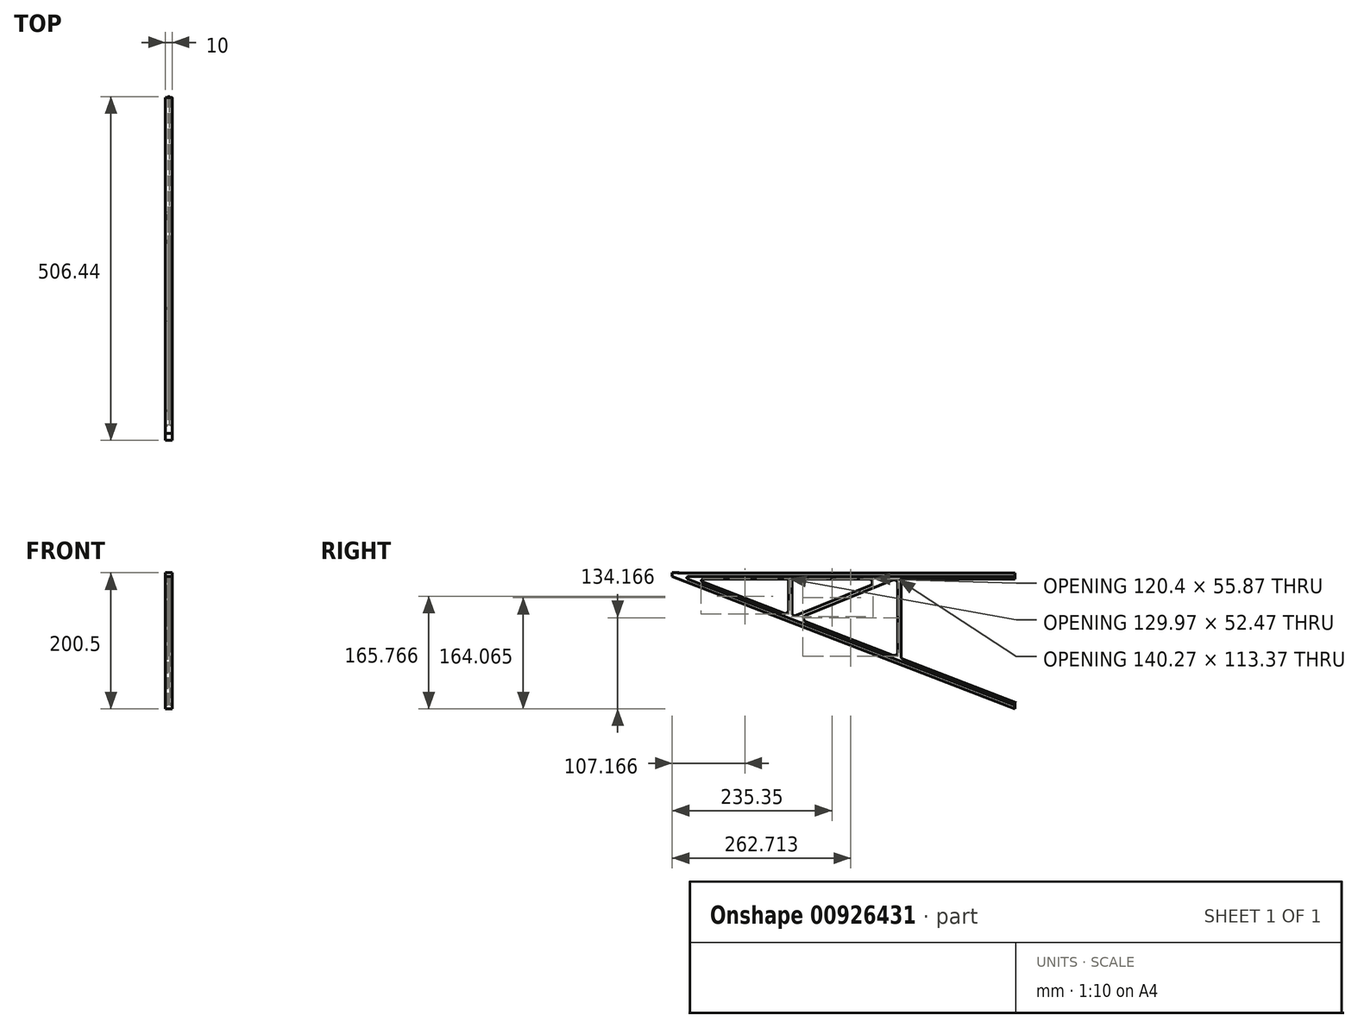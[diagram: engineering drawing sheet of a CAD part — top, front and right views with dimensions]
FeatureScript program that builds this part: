
annotation { "Feature Type Name" : "Feature", "Feature Type Description" : "" }
export const myFeature = defineFeature(function(context is Context, id is Id, definition is map)
    precondition{}
    {
        {
            var Q0;
            Q0=qCreatedBy(makeId("Front.planeOp"),FACE);
            var sketch = newSketch(context, id + "F0", { "sketchPlane" : qUnion([Q0])});
            skLineSegment(sketch, "E0", {"start": v(0, 0) * mm, "end": v(-5, 0) * mm});
            skLineSegment(sketch, "E1.MirrorCS", {"start": v(0, 0) * mm, "end": v(5, 0) * mm});
            skLineSegment(sketch, "E2", {"start": v(5, 0) * mm, "end": v(5, -200) * mm});
            skLineSegment(sketch, "E3.MirrorCS", {"start": v(-5, 0) * mm, "end": v(-5, -200) * mm});
            skLineSegment(sketch, "E4", {"start": v(5, -200) * mm, "end": v(-5, -200) * mm});
            skPoint(sketch, "E5", {"position": v(5, 0) * mm});
            skPoint(sketch, "E6", {"position": v(-5, 0) * mm});
            skSolve(sketch);
        }
        {
            var Q0;
            Q0=makeQuery(id+"F0.imprint","IMPRINT",FACE,{"disambiguationData":[TD([[makeQuery(id+"F0.imprint","IMPRINT",EDGE,{"derivedFrom":sQuery(id+"F0.wireOp",EDGE,"E0")}),1.0]])]});
            extrude(context, id + "F1", {"entities" : qUnion([Q0]), "depth" : 505 * mm, "offsetDistance" : 25 * mm});
        }
        {
            var Q0;
            Q0=qSketchRegion(id+"F0",true);
            extrude(context, id + "F2", {"entities" : qUnion([Q0]), "operationType" : NewBodyOperationType.ADD, "depth" : 500.5 * mm, "offsetDistance" : 25 * mm});
        }
        {
            var Q0;
            Q0=makeQuery(id+"F1.opExtrude","SWEPT_FACE",FACE,{"disambiguationData":[OSD([sQuery(id+"F0.wireOp",EDGE,"E3.MirrorCS")])]});
            var sketch = newSketch(context, id + "F3", { "sketchPlane" : qUnion([Q0])});
            skLineSegment(sketch, "E7", {"start": v(505, 0) * mm, "end": v(505, -5) * mm});
            skLineSegment(sketch, "E8", {"start": v(0, 0) * mm, "end": v(0, -5) * mm});
            skLineSegment(sketch, "E9", {"start": v(0, -5) * mm, "end": v(505, -5) * mm});
            skLineSegment(sketch, "E10", {"start": v(0, -200) * mm, "end": v(0, -195) * mm});
            skLineSegment(sketch, "E11", {"start": v(0, -195) * mm, "end": v(505, 0) * mm});
            skLineSegment(sketch, "E12", {"start": v(0, -200) * mm, "end": v(505, -5) * mm});
            skPoint(sketch, "E13", {"position": v(492.05, -5) * mm});
            skLineSegment(sketch, "E14", {"start": v(492.05, -5) * mm, "end": v(331.35, -5) * mm});
            skLineSegment(sketch, "E15", {"start": v(331.35, -5) * mm, "end": v(333.85, -5) * mm});
            skLineSegment(sketch, "E16", {"start": v(331.35, -5) * mm, "end": v(328.85, -5) * mm});
            skLineSegment(sketch, "E17", {"start": v(328.85, -5) * mm, "end": v(328.85, -68.02) * mm});
            skLineSegment(sketch, "E18", {"start": v(333.85, -5) * mm, "end": v(333.85, -66.09) * mm});
            skLineSegment(sketch, "E19", {"start": v(331.35, -5) * mm, "end": v(170.65, -5) * mm});
            skLineSegment(sketch, "E20", {"start": v(170.65, -5) * mm, "end": v(173.15, -5) * mm});
            skLineSegment(sketch, "E21", {"start": v(170.65, -5) * mm, "end": v(168.15, -5) * mm});
            skLineSegment(sketch, "E22", {"start": v(168.15, -5) * mm, "end": v(168.15, -130.07) * mm});
            skLineSegment(sketch, "E23", {"start": v(173.15, -5) * mm, "end": v(173.15, -128.14) * mm});
            skLineSegment(sketch, "E24", {"start": v(331.35, -5) * mm, "end": v(331.35, -83.15) * mm});
            skLineSegment(sketch, "E25", {"start": v(173.15, -5) * mm, "end": v(328.85, -68.02) * mm});
            skLineSegment(sketch, "E26", {"start": v(328.85, -68.02) * mm, "end": v(331.35, -69.03) * mm});
            skLineSegment(sketch, "E27", {"start": v(328.85, -68.02) * mm, "end": v(327.91, -70.34) * mm});
            skLineSegment(sketch, "E28", {"start": v(327.91, -70.34) * mm, "end": v(328.85, -68.02) * mm});
            skLineSegment(sketch, "E29", {"start": v(328.85, -68.02) * mm, "end": v(329.79, -65.7) * mm});
            skLineSegment(sketch, "E30", {"start": v(173.15, -5) * mm, "end": v(174.09, -2.68) * mm});
            skLineSegment(sketch, "E31", {"start": v(173.15, -5) * mm, "end": v(172.21, -7.32) * mm});
            skLineSegment(sketch, "E32", {"start": v(174.09, -2.68) * mm, "end": v(329.79, -65.7) * mm});
            skLineSegment(sketch, "E33", {"start": v(172.21, -7.32) * mm, "end": v(327.91, -70.34) * mm});
            skSolve(sketch);
        }
        {
            var Q0;
            {var subQ0=sQuery(id+"F3.wireOp",EDGE,"E17");var subQ1=sQuery(id+"F3.wireOp",EDGE,"E9");var subQ2=makeQuery(id+"F3.imprint","INTERSECT",VERTEX,{"derivedFrom":[subQ1,subQ0]});Q0=makeQuery(id+"F3.imprint","IMPRINT",FACE,{"disambiguationData":[TD([[makeQuery(id+"F3.imprint","IMPRINT",EDGE,{"disambiguationData":[TD([[subQ2,1.0]])],"derivedFrom":subQ1}),-1.0]])]});}
            var Q1;
            {var subQ0=sQuery(id+"F3.wireOp",EDGE,"E23");var subQ1=sQuery(id+"F3.wireOp",EDGE,"E11");var subQ2=makeQuery(id+"F3.imprint","INTERSECT",VERTEX,{"derivedFrom":[subQ1,subQ0]});Q1=makeQuery(id+"F3.imprint","IMPRINT",FACE,{"disambiguationData":[TD([[makeQuery(id+"F3.imprint","IMPRINT",EDGE,{"disambiguationData":[TD([[subQ2,-1.0]])],"derivedFrom":subQ1}),1.0]])]});}
            var Q2;
            {var subQ3=sQuery(id+"F3.wireOp",EDGE,"E22");Q2=makeQuery(id+"F3.imprint","IMPRINT",FACE,{"disambiguationData":[TD([[makeQuery(id+"F3.imprint","IMPRINT",EDGE,{"derivedFrom":subQ3}),-1.0]])]});}
            var Q3;
            {var subQ0=sQuery(id+"F3.wireOp",EDGE,"E18");Q3=makeQuery(id+"F3.imprint","IMPRINT",FACE,{"disambiguationData":[TD([[makeQuery(id+"F3.imprint","IMPRINT",EDGE,{"derivedFrom":subQ0}),1.0]])]});}
            extrude(context, id + "F4", {"entities" : qUnion([Q0, Q1, Q2, Q3]), "operationType" : NewBodyOperationType.REMOVE, "endBound" : BoundingType.UP_TO_NEXT, "oppositeDirection" : true, "depth" : 25 * mm, "offsetDistance" : 25 * mm});
        }
        {
            var Q0;
            {var subQ1=sQuery(id+"F0.wireOp",EDGE,"E3.MirrorCS");var subQ2=makeQuery(id+"F1.opExtrude","SWEPT_EDGE",EDGE,{"disambiguationData":[OSD([subQ1,sQuery(id+"F0.wireOp",EDGE,"E4")])]});Q0=makeQuery(id+"F3.imprint","IMPRINT",FACE,{"disambiguationData":[TD([[makeQuery(id+"F3.imprint","IMPRINT",EDGE,{"derivedFrom":subQ2}),-1.0]])]});}
            extrude(context, id + "F5", {"entities" : qUnion([Q0]), "operationType" : NewBodyOperationType.REMOVE, "endBound" : BoundingType.UP_TO_NEXT, "oppositeDirection" : true, "depth" : 25 * mm, "offsetDistance" : 25 * mm});
        }
        {
            var Q0;
            Q0=makeQuery(id+"F1.opExtrude","SWEPT_FACE",FACE,{"disambiguationData":[OSD([sQuery(id+"F0.wireOp",EDGE,"E3.MirrorCS")])]});
            var sketch = newSketch(context, id + "F6", { "sketchPlane" : qUnion([Q0])});
            skLineSegment(sketch, "E34", {"start": v(168.15, -5) * mm, "end": v(179.81, -5) * mm});
            skLineSegment(sketch, "E35", {"start": v(328.85, -5) * mm, "end": v(333.85, -5) * mm});
            skLineSegment(sketch, "E36", {"start": v(325.44, -69.33) * mm, "end": v(333.85, -66.09) * mm});
            skLineSegment(sketch, "E37", {"start": v(168.15, -130.07) * mm, "end": v(173.15, -128.14) * mm});
            skSolve(sketch);
        }
        {
            var Q0;
            Q0=makeQuery(id+"F6.imprint","IMPRINT",FACE,{"disambiguationData":[TD([[makeQuery(id+"F6.imprint","IMPRINT",EDGE,{"derivedFrom":sQuery(id+"F6.wireOp",EDGE,"E34")}),-1.0]])]});
            extrude(context, id + "F7", {"entities" : qUnion([Q0]), "operationType" : NewBodyOperationType.REMOVE, "oppositeDirection" : true, "depth" : 3.5 * mm, "offsetDistance" : 25 * mm});
        }
        {
            var Q0;
            Q0=makeQuery(id+"F1.opExtrude","SWEPT_FACE",FACE,{"disambiguationData":[OSD([sQuery(id+"F0.wireOp",EDGE,"E0"),sQuery(id+"F0.wireOp",EDGE,"E1.MirrorCS")])]});
            var sketch = newSketch(context, id + "F8", { "sketchPlane" : qUnion([Q0])});
            skLineSegment(sketch, "E38.bottom", {"start": v(-5, -505) * mm, "end": v(5, -505) * mm});
            skLineSegment(sketch, "E38.top", {"start": v(-5, -495) * mm, "end": v(5, -495) * mm});
            skLineSegment(sketch, "E38.left", {"start": v(-5, -505) * mm, "end": v(-5, -495) * mm});
            skLineSegment(sketch, "E38.right", {"start": v(5, -505) * mm, "end": v(5, -495) * mm});
            skSolve(sketch);
        }
        {
            var Q0;
            Q0=makeQuery(id+"F1.opExtrude","SWEPT_FACE",FACE,{"disambiguationData":[OSD([sQuery(id+"F0.wireOp",EDGE,"E2")])]});
            var sketch = newSketch(context, id + "F9", { "sketchPlane" : qUnion([Q0])});
            skLineSegment(sketch, "E39", {"start": v(-173.15, -128.14) * mm, "end": v(-168.15, -130.07) * mm});
            skLineSegment(sketch, "E40", {"start": v(-325.44, -69.33) * mm, "end": v(-333.85, -66.09) * mm});
            skLineSegment(sketch, "E41", {"start": v(-333.85, -5) * mm, "end": v(-328.85, -5) * mm});
            skLineSegment(sketch, "E42", {"start": v(-168.15, -5) * mm, "end": v(-179.81, -5) * mm});
            skSolve(sketch);
        }
        {
            var Q0;
            Q0=makeQuery(id+"F8.imprint","IMPRINT",FACE,{"disambiguationData":[TD([[makeQuery(id+"F8.imprint","IMPRINT",EDGE,{"derivedFrom":sQuery(id+"F8.wireOp",EDGE,"E38.bottom")}),1.0]])]});
            extrude(context, id + "F10", {"entities" : qUnion([Q0]), "operationType" : NewBodyOperationType.ADD, "depth" : 0.5 * mm, "offsetDistance" : 25 * mm});
        }
        {
            var Q0;
            Q0=makeQuery(id+"F9.imprint","IMPRINT",FACE,{"disambiguationData":[TD([[makeQuery(id+"F9.imprint","IMPRINT",EDGE,{"derivedFrom":sQuery(id+"F9.wireOp",EDGE,"E39")}),1.0]])]});
            extrude(context, id + "F11", {"entities" : qUnion([Q0]), "operationType" : NewBodyOperationType.REMOVE, "oppositeDirection" : true, "depth" : 3.5 * mm, "offsetDistance" : 25 * mm});
        }
        {
            var Q0;
            {var subQ0=sQuery(id+"F3.wireOp",EDGE,"E9");Q0=makeQuery(id+"F11.boolean.opBoolean","MERGE",FACE,{"derivedFrom":[makeQuery(id+"F7.boolean.opBoolean","MERGE",FACE,{"derivedFrom":[makeQuery(id+"F4.boolean.opBoolean","COPY",FACE,{"derivedFrom":makeQuery(id+"F4.opExtrude","SWEPT_FACE",FACE,{"disambiguationData":[OSD([subQ0]),TDD([makeQuery(id+"F3.imprint","IMPRINT",EDGE,{"disambiguationData":[TD([[makeQuery(id+"F3.imprint","INTERSECT",VERTEX,{"derivedFrom":[subQ0,sQuery(id+"F3.wireOp",EDGE,"E22")]}),1.0]])],"derivedFrom":subQ0})])]})}),makeQuery(id+"F4.boolean.opBoolean","COPY",FACE,{"derivedFrom":makeQuery(id+"F4.opExtrude","SWEPT_FACE",FACE,{"disambiguationData":[OSD([subQ0]),TDD([makeQuery(id+"F3.imprint","IMPRINT",EDGE,{"disambiguationData":[TD([[makeQuery(id+"F3.imprint","INTERSECT",VERTEX,{"derivedFrom":[subQ0,sQuery(id+"F3.wireOp",EDGE,"E18")]}),-1.0]])],"derivedFrom":subQ0})])]})}),makeQuery(id+"F4.boolean.opBoolean","COPY",FACE,{"derivedFrom":makeQuery(id+"F4.opExtrude","SWEPT_FACE",FACE,{"disambiguationData":[OSD([subQ0]),TDD([makeQuery(id+"F3.imprint","IMPRINT",EDGE,{"disambiguationData":[TD([[makeQuery(id+"F3.imprint","INTERSECT",VERTEX,{"derivedFrom":[subQ0,sQuery(id+"F3.wireOp",EDGE,"E17")]}),1.0]])],"derivedFrom":subQ0})])]})})],"fromTools":[makeQuery(id+"F7.opExtrude","SWEPT_FACE",FACE,{"disambiguationData":[OSD([sQuery(id+"F6.wireOp",EDGE,"E34")])]}),makeQuery(id+"F7.opExtrude","SWEPT_FACE",FACE,{"disambiguationData":[OSD([sQuery(id+"F6.wireOp",EDGE,"E35")])]})]})],"fromTools":[makeQuery(id+"F11.opExtrude","SWEPT_FACE",FACE,{"disambiguationData":[OSD([sQuery(id+"F9.wireOp",EDGE,"E41")])]}),makeQuery(id+"F11.opExtrude","SWEPT_FACE",FACE,{"disambiguationData":[OSD([sQuery(id+"F9.wireOp",EDGE,"E42")])]})]});}
            var sketch = newSketch(context, id + "F12", { "sketchPlane" : qUnion([Q0])});
            skLineSegment(sketch, "E43", {"start": v(1.5, 0) * mm, "end": v(1.5, 492.05) * mm});
            skLineSegment(sketch, "E44", {"start": v(-1.5, 0) * mm, "end": v(1.5, 0) * mm});
            skLineSegment(sketch, "E45", {"start": v(-1.5, 0) * mm, "end": v(-1.5, 492.05) * mm});
            skLineSegment(sketch, "E46", {"start": v(1.5, 492.05) * mm, "end": v(-1.5, 492.05) * mm});
            skSolve(sketch);
        }
        {
            var Q0;
            {var subQ3=sQuery(id+"F12.wireOp",EDGE,"E46");Q0=makeQuery(id+"F12.imprint","IMPRINT",FACE,{"disambiguationData":[TD([[makeQuery(id+"F12.imprint","IMPRINT",EDGE,{"derivedFrom":subQ3}),1.0]])]});}
            var Q1;
            {var subQ1=sQuery(id+"F3.wireOp",EDGE,"E9");var subQ2=makeQuery(id+"F4.boolean.opBoolean","COPY",EDGE,{"derivedFrom":makeQuery(id+"F4.opExtrude","SWEPT_EDGE",EDGE,{"disambiguationData":[OSD([subQ1,sQuery(id+"F3.wireOp",EDGE,"E17")])]})});Q1=makeQuery(id+"F12.imprint","IMPRINT",FACE,{"disambiguationData":[TD([[makeQuery(id+"F12.imprint","IMPRINT",EDGE,{"derivedFrom":subQ2}),1.0]])]});}
            var Q2;
            {var subQ3=sQuery(id+"F12.wireOp",EDGE,"E44");Q2=makeQuery(id+"F12.imprint","IMPRINT",FACE,{"disambiguationData":[TD([[makeQuery(id+"F12.imprint","IMPRINT",EDGE,{"derivedFrom":subQ3}),-1.0]])]});}
            extrude(context, id + "F13", {"entities" : qUnion([Q0, Q1, Q2]), "operationType" : NewBodyOperationType.ADD, "depth" : 4 * mm, "offsetDistance" : 25 * mm});
        }
        {
            var Q0;
            {var subQ0=sQuery(id+"F3.wireOp",EDGE,"E11");Q0=makeQuery(id+"F11.boolean.opBoolean","MERGE",FACE,{"derivedFrom":[makeQuery(id+"F7.boolean.opBoolean","MERGE",FACE,{"derivedFrom":[makeQuery(id+"F4.boolean.opBoolean","COPY",FACE,{"derivedFrom":makeQuery(id+"F4.opExtrude","SWEPT_FACE",FACE,{"disambiguationData":[OSD([subQ0]),TDD([makeQuery(id+"F3.imprint","IMPRINT",EDGE,{"disambiguationData":[TD([[makeQuery(id+"F3.imprint","INTERSECT",VERTEX,{"derivedFrom":[subQ0,sQuery(id+"F3.wireOp",EDGE,"E22")]}),1.0]])],"derivedFrom":subQ0})])]})}),makeQuery(id+"F4.boolean.opBoolean","COPY",FACE,{"derivedFrom":makeQuery(id+"F4.opExtrude","SWEPT_FACE",FACE,{"disambiguationData":[OSD([subQ0]),TDD([makeQuery(id+"F3.imprint","IMPRINT",EDGE,{"disambiguationData":[TD([[makeQuery(id+"F3.imprint","INTERSECT",VERTEX,{"derivedFrom":[subQ0,sQuery(id+"F3.wireOp",EDGE,"E18")]}),-1.0]])],"derivedFrom":subQ0})])]})}),makeQuery(id+"F4.boolean.opBoolean","COPY",FACE,{"derivedFrom":makeQuery(id+"F4.opExtrude","SWEPT_FACE",FACE,{"disambiguationData":[OSD([subQ0]),TDD([makeQuery(id+"F3.imprint","IMPRINT",EDGE,{"disambiguationData":[TD([[makeQuery(id+"F3.imprint","INTERSECT",VERTEX,{"derivedFrom":[subQ0,sQuery(id+"F3.wireOp",EDGE,"E23")]}),-1.0]])],"derivedFrom":subQ0})])]})})],"fromTools":[makeQuery(id+"F7.opExtrude","SWEPT_FACE",FACE,{"disambiguationData":[OSD([sQuery(id+"F6.wireOp",EDGE,"E36")])]}),makeQuery(id+"F7.opExtrude","SWEPT_FACE",FACE,{"disambiguationData":[OSD([sQuery(id+"F6.wireOp",EDGE,"E37")])]})]})],"fromTools":[makeQuery(id+"F11.opExtrude","SWEPT_FACE",FACE,{"disambiguationData":[OSD([sQuery(id+"F9.wireOp",EDGE,"E39")])]}),makeQuery(id+"F11.opExtrude","SWEPT_FACE",FACE,{"disambiguationData":[OSD([sQuery(id+"F9.wireOp",EDGE,"E40")])]})]});}
            var sketch = newSketch(context, id + "F14", { "sketchPlane" : qUnion([Q0])});
            skLineSegment(sketch, "E47", {"start": v(-1.5, 70.24) * mm, "end": v(-1.5, -457.22) * mm});
            skLineSegment(sketch, "E48", {"start": v(1.5, 70.24) * mm, "end": v(1.5, -457.22) * mm});
            skLineSegment(sketch, "E49", {"start": v(1.5, -457.22) * mm, "end": v(-1.5, -457.22) * mm});
            skLineSegment(sketch, "E50", {"start": v(1.5, 70.24) * mm, "end": v(-1.5, 70.24) * mm});
            skSolve(sketch);
        }
        {
            var Q0;
            {var subQ3=sQuery(id+"F14.wireOp",EDGE,"E50");Q0=makeQuery(id+"F14.imprint","IMPRINT",FACE,{"disambiguationData":[TD([[makeQuery(id+"F14.imprint","IMPRINT",EDGE,{"derivedFrom":subQ3}),1.0]])]});}
            var Q1;
            {var subQ1=sQuery(id+"F3.wireOp",EDGE,"E11");var subQ2=makeQuery(id+"F4.boolean.opBoolean","COPY",EDGE,{"derivedFrom":makeQuery(id+"F4.opExtrude","SWEPT_EDGE",EDGE,{"disambiguationData":[OSD([subQ1,sQuery(id+"F3.wireOp",EDGE,"E23")])]})});Q1=makeQuery(id+"F14.imprint","IMPRINT",FACE,{"disambiguationData":[TD([[makeQuery(id+"F14.imprint","IMPRINT",EDGE,{"derivedFrom":subQ2}),1.0]])]});}
            var Q2;
            {var subQ1=sQuery(id+"F3.wireOp",EDGE,"E18");var subQ2=sQuery(id+"F3.wireOp",EDGE,"E11");var subQ3=makeQuery(id+"F4.boolean.opBoolean","COPY",EDGE,{"derivedFrom":makeQuery(id+"F4.opExtrude","SWEPT_EDGE",EDGE,{"disambiguationData":[OSD([subQ2,subQ1])]})});Q2=makeQuery(id+"F14.imprint","IMPRINT",FACE,{"disambiguationData":[TD([[makeQuery(id+"F14.imprint","IMPRINT",EDGE,{"derivedFrom":subQ3}),1.0]])]});}
            extrude(context, id + "F15", {"entities" : qUnion([Q0, Q1, Q2]), "operationType" : NewBodyOperationType.ADD, "depth" : 4 * mm, "offsetDistance" : 25 * mm});
        }
        {
            var Q0;
            Q0=makeQuery(id+"F15.opExtrude","SWEPT_FACE",FACE,{"disambiguationData":[OSD([sQuery(id+"F3.wireOp",EDGE,"E11"),sQuery(id+"F3.wireOp",EDGE,"E22")])]});
            extrude(context, id + "F16", {"entities" : qUnion([Q0]), "operationType" : NewBodyOperationType.ADD, "depth" : 40 * mm, "offsetDistance" : 25 * mm});
        }
        {
            var Q0;
            {var subQ0=sQuery(id+"F12.wireOp",EDGE,"E46");var subQ1=sQuery(id+"F12.wireOp",EDGE,"E45");var subQ2=sQuery(id+"F12.wireOp",EDGE,"E43");var subQ3=sQuery(id+"F3.wireOp",EDGE,"E18");var subQ4=sQuery(id+"F3.wireOp",EDGE,"E9");Q0=makeQuery(id+"F15.boolean.opBoolean","INTERSECT",EDGE,{"derivedFrom":[makeQuery(id+"F13.opExtrude","CAP_FACE",FACE,{"disambiguationData":[OSD([subQ4,subQ3,subQ2,subQ1,subQ0])],"isStart":false}),makeQuery(id+"F15.opExtrude","CAP_FACE",FACE,{"disambiguationData":[OSD([subQ4,sQuery(id+"F3.wireOp",EDGE,"E11"),subQ3,sQuery(id+"F6.wireOp",EDGE,"E36"),sQuery(id+"F6.wireOp",EDGE,"E37"),sQuery(id+"F9.wireOp",EDGE,"E39"),sQuery(id+"F9.wireOp",EDGE,"E40"),subQ2,subQ1,subQ0,sQuery(id+"F14.wireOp",EDGE,"E47"),sQuery(id+"F14.wireOp",EDGE,"E48")])],"isStart":false})]});}
            var Q1;
            {var subQ6=sQuery(id+"F3.wireOp",EDGE,"E11");var subQ7=sQuery(id+"F3.wireOp",EDGE,"E9");var subQ10=makeQuery(id+"F4.boolean.opBoolean","COPY",EDGE,{"derivedFrom":makeQuery(id+"F4.opExtrude","SWEPT_EDGE",EDGE,{"disambiguationData":[OSD([subQ7,subQ6])]})});var subQ11=sQuery(id+"F0.wireOp",EDGE,"E3.MirrorCS");Q1=makeQuery(id+"F13.boolean.opBoolean","SPLIT",EDGE,{"disambiguationData":[TD([makeQuery(id+"F1.opExtrude","SWEPT_FACE",FACE,{"disambiguationData":[OSD([subQ11])]})])],"derivedFrom":subQ10});}
            var Q2;
            {var subQ1=sQuery(id+"F3.wireOp",EDGE,"E11");var subQ9=sQuery(id+"F3.wireOp",EDGE,"E9");var subQ13=makeQuery(id+"F4.boolean.opBoolean","COPY",EDGE,{"derivedFrom":makeQuery(id+"F4.opExtrude","SWEPT_EDGE",EDGE,{"disambiguationData":[OSD([subQ9,subQ1])]})});Q2=makeQuery(id+"F13.boolean.opBoolean","SPLIT",EDGE,{"disambiguationData":[TD([makeQuery(id+"F1.opExtrude","SWEPT_FACE",FACE,{"disambiguationData":[OSD([sQuery(id+"F0.wireOp",EDGE,"E2")])]})])],"derivedFrom":subQ13});}
            fillet(context, id + "F17", {"entities" : qUnion([Q0, Q1, Q2]), "radius" : 2 * mm, "tangentPropagation" : true, "allowEdgeOverflow" : false});
        }
        {
            var Q0;
            Q0=makeQuery(id+"F13.opExtrude","CAP_EDGE",EDGE,{"disambiguationData":[OSD([sQuery(id+"F3.wireOp",EDGE,"E9"),sQuery(id+"F3.wireOp",EDGE,"E18")])],"isStart":false});
            var Q1;
            Q1=makeQuery(id+"F13.opExtrude","CAP_EDGE",EDGE,{"disambiguationData":[OSD([sQuery(id+"F3.wireOp",EDGE,"E9"),sQuery(id+"F3.wireOp",EDGE,"E17")])],"isStart":false});
            var Q2;
            Q2=makeQuery(id+"F4.boolean.opBoolean","COPY",EDGE,{"derivedFrom":makeQuery(id+"F4.opExtrude","SWEPT_EDGE",EDGE,{"disambiguationData":[OSD([sQuery(id+"F3.wireOp",EDGE,"E17"),sQuery(id+"F3.wireOp",EDGE,"E32")])]})});
            var Q3;
            {var subQ0=sQuery(id+"F3.wireOp",EDGE,"E18");Q3=makeQuery(id+"F15.boolean.opBoolean","INTERSECT",EDGE,{"derivedFrom":[makeQuery(id+"F4.boolean.opBoolean","COPY",FACE,{"derivedFrom":makeQuery(id+"F4.opExtrude","SWEPT_FACE",FACE,{"disambiguationData":[OSD([subQ0])]})}),makeQuery(id+"F15.opExtrude","CAP_FACE",FACE,{"disambiguationData":[OSD([sQuery(id+"F3.wireOp",EDGE,"E9"),sQuery(id+"F3.wireOp",EDGE,"E11"),subQ0,sQuery(id+"F6.wireOp",EDGE,"E36"),sQuery(id+"F6.wireOp",EDGE,"E37"),sQuery(id+"F9.wireOp",EDGE,"E39"),sQuery(id+"F9.wireOp",EDGE,"E40"),sQuery(id+"F12.wireOp",EDGE,"E43"),sQuery(id+"F12.wireOp",EDGE,"E45"),sQuery(id+"F12.wireOp",EDGE,"E46"),sQuery(id+"F14.wireOp",EDGE,"E47"),sQuery(id+"F14.wireOp",EDGE,"E48")])],"isStart":false})]});}
            var Q4;
            {var subQ0=sQuery(id+"F3.wireOp",EDGE,"E32");Q4=makeQuery(id+"F13.boolean.opBoolean","INTERSECT",EDGE,{"derivedFrom":[makeQuery(id+"F4.boolean.opBoolean","COPY",FACE,{"derivedFrom":makeQuery(id+"F4.opExtrude","SWEPT_FACE",FACE,{"disambiguationData":[OSD([subQ0])]})}),makeQuery(id+"F13.opExtrude","CAP_FACE",FACE,{"disambiguationData":[OSD([sQuery(id+"F3.wireOp",EDGE,"E9"),sQuery(id+"F3.wireOp",EDGE,"E17"),subQ0,sQuery(id+"F12.wireOp",EDGE,"E43"),sQuery(id+"F12.wireOp",EDGE,"E45")])],"isStart":false})]});}
            var Q5;
            Q5=makeQuery(id+"F4.boolean.opBoolean","COPY",EDGE,{"derivedFrom":makeQuery(id+"F4.opExtrude","SWEPT_EDGE",EDGE,{"disambiguationData":[OSD([sQuery(id+"F3.wireOp",EDGE,"E23"),sQuery(id+"F3.wireOp",EDGE,"E33")])]})});
            var Q6;
            Q6=makeQuery(id+"F13.opExtrude","CAP_EDGE",EDGE,{"disambiguationData":[OSD([sQuery(id+"F3.wireOp",EDGE,"E9"),sQuery(id+"F3.wireOp",EDGE,"E22")])],"isStart":false});
            var Q7;
            {var subQ0=sQuery(id+"F3.wireOp",EDGE,"E23");Q7=makeQuery(id+"F15.boolean.opBoolean","INTERSECT",EDGE,{"derivedFrom":[makeQuery(id+"F4.boolean.opBoolean","COPY",FACE,{"derivedFrom":makeQuery(id+"F4.opExtrude","SWEPT_FACE",FACE,{"disambiguationData":[OSD([subQ0])]})}),makeQuery(id+"F15.opExtrude","CAP_FACE",FACE,{"disambiguationData":[OSD([sQuery(id+"F3.wireOp",EDGE,"E11"),subQ0,sQuery(id+"F3.wireOp",EDGE,"E33"),sQuery(id+"F14.wireOp",EDGE,"E47"),sQuery(id+"F14.wireOp",EDGE,"E48")])],"isStart":false})]});}
            var Q8;
            {var subQ0=sQuery(id+"F3.wireOp",EDGE,"E22");var subQ1=sQuery(id+"F3.wireOp",EDGE,"E11");Q8=makeQuery(id+"F16.boolean.opBoolean","INTERSECT",EDGE,{"derivedFrom":[makeQuery(id+"F4.boolean.opBoolean","COPY",FACE,{"derivedFrom":makeQuery(id+"F4.opExtrude","SWEPT_FACE",FACE,{"disambiguationData":[OSD([subQ0])]})}),makeQuery(id+"F16.opExtrude","SWEPT_FACE",FACE,{"disambiguationData":[OSD([subQ1,subQ0]),TDD([makeQuery(id+"F15.opExtrude","CAP_EDGE",EDGE,{"disambiguationData":[OSD([subQ1,subQ0])],"isStart":false})])]})]});}
            var Q9;
            {var subQ0=sQuery(id+"F3.wireOp",EDGE,"E33");Q9=makeQuery(id+"F15.boolean.opBoolean","INTERSECT",EDGE,{"derivedFrom":[makeQuery(id+"F4.boolean.opBoolean","COPY",FACE,{"derivedFrom":makeQuery(id+"F4.opExtrude","SWEPT_FACE",FACE,{"disambiguationData":[OSD([subQ0])]})}),makeQuery(id+"F15.opExtrude","CAP_FACE",FACE,{"disambiguationData":[OSD([sQuery(id+"F3.wireOp",EDGE,"E11"),sQuery(id+"F3.wireOp",EDGE,"E23"),subQ0,sQuery(id+"F14.wireOp",EDGE,"E47"),sQuery(id+"F14.wireOp",EDGE,"E48")])],"isStart":false})]});}
            fillet(context, id + "F18", {"entities" : qUnion([Q0, Q1, Q2, Q3, Q4, Q5, Q6, Q7, Q8, Q9]), "radius" : 5 * mm, "tangentPropagation" : true, "allowEdgeOverflow" : false});
        }
        {
            var Q0;
            {var subQ0=sQuery(id+"F14.wireOp",EDGE,"E47");var subQ1=sQuery(id+"F3.wireOp",EDGE,"E22");var subQ2=sQuery(id+"F3.wireOp",EDGE,"E11");var subQ5=sQuery(id+"F3.wireOp",EDGE,"E18");var subQ7=sQuery(id+"F12.wireOp",EDGE,"E45");var subQ8=sQuery(id+"F3.wireOp",EDGE,"E9");var subQ9=sQuery(id+"F6.wireOp",EDGE,"E37");var subQ10=sQuery(id+"F6.wireOp",EDGE,"E36");var subQ11=sQuery(id+"F3.wireOp",EDGE,"E23");var subQ13=makeQuery(id+"F11.boolean.opBoolean","MERGE",FACE,{"derivedFrom":[makeQuery(id+"F7.boolean.opBoolean","MERGE",FACE,{"derivedFrom":[makeQuery(id+"F4.boolean.opBoolean","COPY",FACE,{"derivedFrom":makeQuery(id+"F4.opExtrude","SWEPT_FACE",FACE,{"disambiguationData":[OSD([subQ2]),TDD([makeQuery(id+"F3.imprint","IMPRINT",EDGE,{"disambiguationData":[TD([[makeQuery(id+"F3.imprint","INTERSECT",VERTEX,{"derivedFrom":[subQ2,subQ1]}),1.0]])],"derivedFrom":subQ2})])]})}),makeQuery(id+"F4.boolean.opBoolean","COPY",FACE,{"derivedFrom":makeQuery(id+"F4.opExtrude","SWEPT_FACE",FACE,{"disambiguationData":[OSD([subQ2]),TDD([makeQuery(id+"F3.imprint","IMPRINT",EDGE,{"disambiguationData":[TD([[makeQuery(id+"F3.imprint","INTERSECT",VERTEX,{"derivedFrom":[subQ2,subQ5]}),-1.0]])],"derivedFrom":subQ2})])]})}),makeQuery(id+"F4.boolean.opBoolean","COPY",FACE,{"derivedFrom":makeQuery(id+"F4.opExtrude","SWEPT_FACE",FACE,{"disambiguationData":[OSD([subQ2]),TDD([makeQuery(id+"F3.imprint","IMPRINT",EDGE,{"disambiguationData":[TD([[makeQuery(id+"F3.imprint","INTERSECT",VERTEX,{"derivedFrom":[subQ2,subQ11]}),-1.0]])],"derivedFrom":subQ2})])]})})],"fromTools":[makeQuery(id+"F7.opExtrude","SWEPT_FACE",FACE,{"disambiguationData":[OSD([subQ10])]}),makeQuery(id+"F7.opExtrude","SWEPT_FACE",FACE,{"disambiguationData":[OSD([subQ9])]})]})],"fromTools":[makeQuery(id+"F11.opExtrude","SWEPT_FACE",FACE,{"disambiguationData":[OSD([sQuery(id+"F9.wireOp",EDGE,"E39")])]}),makeQuery(id+"F11.opExtrude","SWEPT_FACE",FACE,{"disambiguationData":[OSD([sQuery(id+"F9.wireOp",EDGE,"E40")])]})]});Q0=makeQuery(id+"F16.boolean.opBoolean","MERGE",EDGE,{"derivedFrom":[makeQuery(id+"F15.boolean.opBoolean","MERGE",EDGE,{"derivedFrom":[makeQuery(id+"F7.boolean.opBoolean","COPY",EDGE,{"derivedFrom":makeQuery(id+"F7.opExtrude","CAP_EDGE",EDGE,{"disambiguationData":[OSD([subQ10])],"isStart":false})}),makeQuery(id+"F7.boolean.opBoolean","COPY",EDGE,{"derivedFrom":makeQuery(id+"F7.opExtrude","CAP_EDGE",EDGE,{"disambiguationData":[OSD([subQ9])],"isStart":false})}),makeQuery(id+"F13.boolean.opBoolean","INTERSECT",EDGE,{"derivedFrom":[subQ13,makeQuery(id+"F13.opExtrude","SWEPT_FACE",FACE,{"disambiguationData":[OSD([subQ7]),TDD([makeQuery(id+"F12.imprint","IMPRINT",EDGE,{"disambiguationData":[TD([[makeQuery(id+"F12.imprint","INTERSECT",VERTEX,{"derivedFrom":[makeQuery(id+"F4.boolean.opBoolean","COPY",EDGE,{"derivedFrom":makeQuery(id+"F4.opExtrude","SWEPT_EDGE",EDGE,{"disambiguationData":[OSD([subQ8,subQ5])]})}),subQ7]}),-1.0]])],"derivedFrom":subQ7})])]})]}),makeQuery(id+"F15.opExtrude","CAP_EDGE",EDGE,{"disambiguationData":[OSD([subQ0]),TDD([makeQuery(id+"F14.imprint","IMPRINT",EDGE,{"disambiguationData":[TD([[makeQuery(id+"F14.imprint","INTERSECT",VERTEX,{"derivedFrom":[makeQuery(id+"F4.boolean.opBoolean","COPY",EDGE,{"derivedFrom":makeQuery(id+"F4.opExtrude","SWEPT_EDGE",EDGE,{"disambiguationData":[OSD([subQ2,subQ11])]})}),subQ0]}),-1.0]])],"derivedFrom":subQ0})])],"isStart":true}),makeQuery(id+"F15.opExtrude","CAP_EDGE",EDGE,{"disambiguationData":[OSD([subQ0]),TDD([makeQuery(id+"F14.imprint","IMPRINT",EDGE,{"disambiguationData":[TD([[makeQuery(id+"F14.imprint","INTERSECT",VERTEX,{"derivedFrom":[makeQuery(id+"F4.boolean.opBoolean","COPY",EDGE,{"derivedFrom":makeQuery(id+"F4.opExtrude","SWEPT_EDGE",EDGE,{"disambiguationData":[OSD([subQ2,subQ5])]})}),subQ0]}),-1.0]])],"derivedFrom":subQ0})])],"isStart":true})]}),makeQuery(id+"F15.opExtrude","CAP_EDGE",EDGE,{"disambiguationData":[OSD([subQ0]),TDD([makeQuery(id+"F14.imprint","IMPRINT",EDGE,{"disambiguationData":[TD([[makeQuery(id+"F14.imprint","INTERSECT",VERTEX,{"derivedFrom":[makeQuery(id+"F4.boolean.opBoolean","COPY",EDGE,{"derivedFrom":makeQuery(id+"F4.opExtrude","SWEPT_EDGE",EDGE,{"disambiguationData":[OSD([subQ2,subQ1])]})}),subQ0]}),1.0]])],"derivedFrom":subQ0})])],"isStart":true})]});}
            var Q1;
            {var subQ0=sQuery(id+"F14.wireOp",EDGE,"E48");var subQ1=sQuery(id+"F3.wireOp",EDGE,"E22");var subQ2=sQuery(id+"F3.wireOp",EDGE,"E11");var subQ3=sQuery(id+"F3.wireOp",EDGE,"E10");var subQ4=sQuery(id+"F0.wireOp",EDGE,"E3.MirrorCS");var subQ5=sQuery(id+"F3.wireOp",EDGE,"E18");var subQ6=sQuery(id+"F12.wireOp",EDGE,"E46");var subQ7=sQuery(id+"F12.wireOp",EDGE,"E43");var subQ8=sQuery(id+"F3.wireOp",EDGE,"E9");var subQ9=sQuery(id+"F9.wireOp",EDGE,"E40");var subQ10=sQuery(id+"F9.wireOp",EDGE,"E39");var subQ11=sQuery(id+"F3.wireOp",EDGE,"E23");var subQ12=sQuery(id+"F3.wireOp",EDGE,"E33");var subQ13=makeQuery(id+"F11.boolean.opBoolean","MERGE",FACE,{"derivedFrom":[makeQuery(id+"F7.boolean.opBoolean","MERGE",FACE,{"derivedFrom":[makeQuery(id+"F4.boolean.opBoolean","COPY",FACE,{"derivedFrom":makeQuery(id+"F4.opExtrude","SWEPT_FACE",FACE,{"disambiguationData":[OSD([subQ2]),TDD([makeQuery(id+"F3.imprint","IMPRINT",EDGE,{"disambiguationData":[TD([[makeQuery(id+"F3.imprint","INTERSECT",VERTEX,{"derivedFrom":[subQ2,subQ1]}),1.0]])],"derivedFrom":subQ2})])]})}),makeQuery(id+"F4.boolean.opBoolean","COPY",FACE,{"derivedFrom":makeQuery(id+"F4.opExtrude","SWEPT_FACE",FACE,{"disambiguationData":[OSD([subQ2]),TDD([makeQuery(id+"F3.imprint","IMPRINT",EDGE,{"disambiguationData":[TD([[makeQuery(id+"F3.imprint","INTERSECT",VERTEX,{"derivedFrom":[subQ2,subQ5]}),-1.0]])],"derivedFrom":subQ2})])]})}),makeQuery(id+"F4.boolean.opBoolean","COPY",FACE,{"derivedFrom":makeQuery(id+"F4.opExtrude","SWEPT_FACE",FACE,{"disambiguationData":[OSD([subQ2]),TDD([makeQuery(id+"F3.imprint","IMPRINT",EDGE,{"disambiguationData":[TD([[makeQuery(id+"F3.imprint","INTERSECT",VERTEX,{"derivedFrom":[subQ2,subQ11]}),-1.0]])],"derivedFrom":subQ2})])]})})],"fromTools":[makeQuery(id+"F7.opExtrude","SWEPT_FACE",FACE,{"disambiguationData":[OSD([sQuery(id+"F6.wireOp",EDGE,"E36")])]}),makeQuery(id+"F7.opExtrude","SWEPT_FACE",FACE,{"disambiguationData":[OSD([sQuery(id+"F6.wireOp",EDGE,"E37")])]})]})],"fromTools":[makeQuery(id+"F11.opExtrude","SWEPT_FACE",FACE,{"disambiguationData":[OSD([subQ10])]}),makeQuery(id+"F11.opExtrude","SWEPT_FACE",FACE,{"disambiguationData":[OSD([subQ9])]})]});Q1=makeQuery(id+"F16.boolean.opBoolean","MERGE",EDGE,{"derivedFrom":[makeQuery(id+"F15.boolean.opBoolean","MERGE",EDGE,{"derivedFrom":[makeQuery(id+"F11.boolean.opBoolean","COPY",EDGE,{"derivedFrom":makeQuery(id+"F11.opExtrude","CAP_EDGE",EDGE,{"disambiguationData":[OSD([subQ10])],"isStart":false})}),makeQuery(id+"F11.boolean.opBoolean","COPY",EDGE,{"derivedFrom":makeQuery(id+"F11.opExtrude","CAP_EDGE",EDGE,{"disambiguationData":[OSD([subQ9])],"isStart":false})}),makeQuery(id+"F13.boolean.opBoolean","INTERSECT",EDGE,{"derivedFrom":[subQ13,makeQuery(id+"F13.opExtrude","SWEPT_FACE",FACE,{"disambiguationData":[OSD([subQ7]),TDD([makeQuery(id+"F12.imprint","IMPRINT",EDGE,{"disambiguationData":[TD([[makeQuery(id+"F12.imprint","INTERSECT",VERTEX,{"derivedFrom":[makeQuery(id+"F4.boolean.opBoolean","COPY",EDGE,{"derivedFrom":makeQuery(id+"F4.opExtrude","SWEPT_EDGE",EDGE,{"disambiguationData":[OSD([subQ8,subQ5])]})}),subQ7]}),-1.0],[makeQuery(id+"F12.imprint","INTERSECT",VERTEX,{"derivedFrom":[makeQuery(id+"F4.boolean.opBoolean","COPY",EDGE,{"derivedFrom":makeQuery(id+"F4.opExtrude","SWEPT_EDGE",EDGE,{"disambiguationData":[OSD([subQ8,subQ2])]})}),subQ7,subQ6]}),1.0]])],"derivedFrom":subQ7})])]})]}),makeQuery(id+"F15.opExtrude","CAP_EDGE",EDGE,{"disambiguationData":[OSD([subQ0]),TDD([makeQuery(id+"F14.imprint","IMPRINT",EDGE,{"disambiguationData":[TD([[makeQuery(id+"F14.imprint","INTERSECT",VERTEX,{"derivedFrom":[makeQuery(id+"F4.boolean.opBoolean","COPY",EDGE,{"derivedFrom":makeQuery(id+"F4.opExtrude","SWEPT_EDGE",EDGE,{"disambiguationData":[OSD([subQ2,subQ11])]})}),subQ0]}),-1.0],[makeQuery(id+"F14.imprint","INTERSECT",VERTEX,{"derivedFrom":[makeQuery(id+"F4.boolean.opBoolean","COPY",EDGE,{"derivedFrom":makeQuery(id+"F4.opExtrude","SWEPT_EDGE",EDGE,{"disambiguationData":[OSD([subQ2,subQ12])]})}),subQ0]}),1.0]])],"derivedFrom":subQ0})])],"isStart":true}),makeQuery(id+"F15.opExtrude","CAP_EDGE",EDGE,{"disambiguationData":[OSD([subQ0]),TDD([makeQuery(id+"F14.imprint","IMPRINT",EDGE,{"disambiguationData":[TD([[makeQuery(id+"F14.imprint","INTERSECT",VERTEX,{"derivedFrom":[makeQuery(id+"F4.boolean.opBoolean","COPY",EDGE,{"derivedFrom":makeQuery(id+"F4.opExtrude","SWEPT_EDGE",EDGE,{"disambiguationData":[OSD([subQ2,subQ5])]})}),subQ0]}),-1.0],[makeQuery(id+"F14.imprint","INTERSECT",VERTEX,{"derivedFrom":[makeQuery(id+"F13.boolean.opBoolean","INTERSECT",EDGE,{"derivedFrom":[subQ13,makeQuery(id+"F13.opExtrude","CAP_FACE",FACE,{"disambiguationData":[OSD([subQ8,subQ5,subQ7,sQuery(id+"F12.wireOp",EDGE,"E45"),subQ6])],"isStart":false})]}),subQ0]}),1.0]])],"derivedFrom":subQ0})])],"isStart":true})]}),makeQuery(id+"F15.opExtrude","CAP_EDGE",EDGE,{"disambiguationData":[OSD([subQ0]),TDD([makeQuery(id+"F14.imprint","IMPRINT",EDGE,{"disambiguationData":[TD([[makeQuery(id+"F14.imprint","INTERSECT",VERTEX,{"derivedFrom":[makeQuery(id+"F4.boolean.opBoolean","COPY",EDGE,{"derivedFrom":makeQuery(id+"F4.opExtrude","SWEPT_EDGE",EDGE,{"disambiguationData":[OSD([subQ2,subQ1])]})}),subQ0]}),1.0],[makeQuery(id+"F14.imprint","INTERSECT",VERTEX,{"derivedFrom":[makeQuery(id+"F4.boolean.opBoolean","COPY",EDGE,{"derivedFrom":makeQuery(id+"F4.opExtrude","SWEPT_EDGE",EDGE,{"disambiguationData":[OSD([subQ4,subQ3,subQ2])]})}),subQ0,sQuery(id+"F14.wireOp",EDGE,"E50")]}),-1.0]])],"derivedFrom":subQ0})])],"isStart":true})]});}
            var Q2;
            {var subQ0=sQuery(id+"F12.wireOp",EDGE,"E43");var subQ1=sQuery(id+"F3.wireOp",EDGE,"E9");Q2=makeQuery(id+"F13.boolean.opBoolean","MERGE",EDGE,{"derivedFrom":[makeQuery(id+"F11.boolean.opBoolean","COPY",EDGE,{"derivedFrom":makeQuery(id+"F11.opExtrude","CAP_EDGE",EDGE,{"disambiguationData":[OSD([sQuery(id+"F9.wireOp",EDGE,"E41")])],"isStart":false})}),makeQuery(id+"F11.boolean.opBoolean","COPY",EDGE,{"derivedFrom":makeQuery(id+"F11.opExtrude","CAP_EDGE",EDGE,{"disambiguationData":[OSD([sQuery(id+"F9.wireOp",EDGE,"E42")])],"isStart":false})}),makeQuery(id+"F13.opExtrude","CAP_EDGE",EDGE,{"disambiguationData":[OSD([subQ0]),TDD([makeQuery(id+"F12.imprint","IMPRINT",EDGE,{"disambiguationData":[TD([[makeQuery(id+"F12.imprint","INTERSECT",VERTEX,{"derivedFrom":[makeQuery(id+"F4.boolean.opBoolean","COPY",EDGE,{"derivedFrom":makeQuery(id+"F4.opExtrude","SWEPT_EDGE",EDGE,{"disambiguationData":[OSD([subQ1,sQuery(id+"F3.wireOp",EDGE,"E22")])]})}),subQ0]}),1.0],[makeQuery(id+"F12.imprint","INTERSECT",VERTEX,{"derivedFrom":[makeQuery(id+"F4.boolean.opBoolean","COPY",EDGE,{"derivedFrom":makeQuery(id+"F4.opExtrude","SWEPT_EDGE",EDGE,{"disambiguationData":[OSD([sQuery(id+"F0.wireOp",EDGE,"E3.MirrorCS"),sQuery(id+"F3.wireOp",EDGE,"E8"),subQ1])]})}),subQ0,sQuery(id+"F12.wireOp",EDGE,"E44")]}),-1.0]])],"derivedFrom":subQ0})])],"isStart":true}),makeQuery(id+"F13.opExtrude","CAP_EDGE",EDGE,{"disambiguationData":[OSD([subQ0]),TDD([makeQuery(id+"F12.imprint","IMPRINT",EDGE,{"disambiguationData":[TD([[makeQuery(id+"F12.imprint","INTERSECT",VERTEX,{"derivedFrom":[makeQuery(id+"F4.boolean.opBoolean","COPY",EDGE,{"derivedFrom":makeQuery(id+"F4.opExtrude","SWEPT_EDGE",EDGE,{"disambiguationData":[OSD([subQ1,sQuery(id+"F3.wireOp",EDGE,"E17")])]})}),subQ0]}),1.0],[makeQuery(id+"F12.imprint","INTERSECT",VERTEX,{"derivedFrom":[makeQuery(id+"F4.boolean.opBoolean","COPY",EDGE,{"derivedFrom":makeQuery(id+"F4.opExtrude","SWEPT_EDGE",EDGE,{"disambiguationData":[OSD([subQ1,sQuery(id+"F3.wireOp",EDGE,"E32")])]})}),subQ0]}),-1.0]])],"derivedFrom":subQ0})])],"isStart":true}),makeQuery(id+"F13.opExtrude","CAP_EDGE",EDGE,{"disambiguationData":[OSD([subQ0]),TDD([makeQuery(id+"F12.imprint","IMPRINT",EDGE,{"disambiguationData":[TD([[makeQuery(id+"F12.imprint","INTERSECT",VERTEX,{"derivedFrom":[makeQuery(id+"F4.boolean.opBoolean","COPY",EDGE,{"derivedFrom":makeQuery(id+"F4.opExtrude","SWEPT_EDGE",EDGE,{"disambiguationData":[OSD([subQ1,sQuery(id+"F3.wireOp",EDGE,"E18")])]})}),subQ0]}),-1.0],[makeQuery(id+"F12.imprint","INTERSECT",VERTEX,{"derivedFrom":[makeQuery(id+"F4.boolean.opBoolean","COPY",EDGE,{"derivedFrom":makeQuery(id+"F4.opExtrude","SWEPT_EDGE",EDGE,{"disambiguationData":[OSD([subQ1,sQuery(id+"F3.wireOp",EDGE,"E11")])]})}),subQ0,sQuery(id+"F12.wireOp",EDGE,"E46")]}),1.0]])],"derivedFrom":subQ0})])],"isStart":true})]});}
            var Q3;
            {var subQ0=sQuery(id+"F12.wireOp",EDGE,"E45");var subQ1=sQuery(id+"F3.wireOp",EDGE,"E9");Q3=makeQuery(id+"F13.boolean.opBoolean","MERGE",EDGE,{"derivedFrom":[makeQuery(id+"F7.boolean.opBoolean","COPY",EDGE,{"derivedFrom":makeQuery(id+"F7.opExtrude","CAP_EDGE",EDGE,{"disambiguationData":[OSD([sQuery(id+"F6.wireOp",EDGE,"E34")])],"isStart":false})}),makeQuery(id+"F7.boolean.opBoolean","COPY",EDGE,{"derivedFrom":makeQuery(id+"F7.opExtrude","CAP_EDGE",EDGE,{"disambiguationData":[OSD([sQuery(id+"F6.wireOp",EDGE,"E35")])],"isStart":false})}),makeQuery(id+"F13.opExtrude","CAP_EDGE",EDGE,{"disambiguationData":[OSD([subQ0]),TDD([makeQuery(id+"F12.imprint","IMPRINT",EDGE,{"disambiguationData":[TD([[makeQuery(id+"F12.imprint","INTERSECT",VERTEX,{"derivedFrom":[makeQuery(id+"F4.boolean.opBoolean","COPY",EDGE,{"derivedFrom":makeQuery(id+"F4.opExtrude","SWEPT_EDGE",EDGE,{"disambiguationData":[OSD([subQ1,sQuery(id+"F3.wireOp",EDGE,"E22")])]})}),subQ0]}),1.0]])],"derivedFrom":subQ0})])],"isStart":true}),makeQuery(id+"F13.opExtrude","CAP_EDGE",EDGE,{"disambiguationData":[OSD([subQ0]),TDD([makeQuery(id+"F12.imprint","IMPRINT",EDGE,{"disambiguationData":[TD([[makeQuery(id+"F12.imprint","INTERSECT",VERTEX,{"derivedFrom":[makeQuery(id+"F4.boolean.opBoolean","COPY",EDGE,{"derivedFrom":makeQuery(id+"F4.opExtrude","SWEPT_EDGE",EDGE,{"disambiguationData":[OSD([subQ1,sQuery(id+"F3.wireOp",EDGE,"E17")])]})}),subQ0]}),1.0]])],"derivedFrom":subQ0})])],"isStart":true}),makeQuery(id+"F13.opExtrude","CAP_EDGE",EDGE,{"disambiguationData":[OSD([subQ0]),TDD([makeQuery(id+"F12.imprint","IMPRINT",EDGE,{"disambiguationData":[TD([[makeQuery(id+"F12.imprint","INTERSECT",VERTEX,{"derivedFrom":[makeQuery(id+"F4.boolean.opBoolean","COPY",EDGE,{"derivedFrom":makeQuery(id+"F4.opExtrude","SWEPT_EDGE",EDGE,{"disambiguationData":[OSD([subQ1,sQuery(id+"F3.wireOp",EDGE,"E18")])]})}),subQ0]}),-1.0]])],"derivedFrom":subQ0})])],"isStart":true})]});}
            var Q4;
            {var subQ0=sQuery(id+"F14.wireOp",EDGE,"E48");var subQ1=sQuery(id+"F3.wireOp",EDGE,"E22");var subQ2=sQuery(id+"F3.wireOp",EDGE,"E11");var subQ3=sQuery(id+"F3.wireOp",EDGE,"E18");var subQ4=sQuery(id+"F12.wireOp",EDGE,"E46");var subQ5=sQuery(id+"F12.wireOp",EDGE,"E43");var subQ6=sQuery(id+"F3.wireOp",EDGE,"E9");var subQ7=sQuery(id+"F9.wireOp",EDGE,"E40");var subQ8=sQuery(id+"F9.wireOp",EDGE,"E39");var subQ9=sQuery(id+"F3.wireOp",EDGE,"E23");var subQ10=sQuery(id+"F3.wireOp",EDGE,"E33");var subQ11=makeQuery(id+"F4.boolean.opBoolean","COPY",FACE,{"derivedFrom":makeQuery(id+"F4.opExtrude","SWEPT_FACE",FACE,{"disambiguationData":[OSD([subQ2]),TDD([makeQuery(id+"F3.imprint","IMPRINT",EDGE,{"disambiguationData":[TD([[makeQuery(id+"F3.imprint","INTERSECT",VERTEX,{"derivedFrom":[subQ2,subQ9]}),-1.0]])],"derivedFrom":subQ2})])]})});var subQ13=makeQuery(id+"F4.boolean.opBoolean","COPY",FACE,{"derivedFrom":makeQuery(id+"F4.opExtrude","SWEPT_FACE",FACE,{"disambiguationData":[OSD([subQ2]),TDD([makeQuery(id+"F3.imprint","IMPRINT",EDGE,{"disambiguationData":[TD([[makeQuery(id+"F3.imprint","INTERSECT",VERTEX,{"derivedFrom":[subQ2,subQ3]}),-1.0]])],"derivedFrom":subQ2})])]})});var subQ14=sQuery(id+"F3.wireOp",EDGE,"E10");var subQ15=sQuery(id+"F0.wireOp",EDGE,"E3.MirrorCS");var subQ17=makeQuery(id+"F4.boolean.opBoolean","COPY",FACE,{"derivedFrom":makeQuery(id+"F4.opExtrude","SWEPT_FACE",FACE,{"disambiguationData":[OSD([subQ2]),TDD([makeQuery(id+"F3.imprint","IMPRINT",EDGE,{"disambiguationData":[TD([[makeQuery(id+"F3.imprint","INTERSECT",VERTEX,{"derivedFrom":[subQ2,subQ1]}),1.0]])],"derivedFrom":subQ2})])]})});var subQ18=makeQuery(id+"F4.boolean.opBoolean","COPY",EDGE,{"derivedFrom":makeQuery(id+"F4.opExtrude","SWEPT_EDGE",EDGE,{"disambiguationData":[OSD([subQ6,subQ2])]})});var subQ19=makeQuery(id+"F13.opExtrude","SWEPT_FACE",FACE,{"disambiguationData":[OSD([subQ5]),TDD([makeQuery(id+"F12.imprint","IMPRINT",EDGE,{"disambiguationData":[TD([[makeQuery(id+"F12.imprint","INTERSECT",VERTEX,{"derivedFrom":[makeQuery(id+"F4.boolean.opBoolean","COPY",EDGE,{"derivedFrom":makeQuery(id+"F4.opExtrude","SWEPT_EDGE",EDGE,{"disambiguationData":[OSD([subQ6,subQ3])]})}),subQ5]}),-1.0],[makeQuery(id+"F12.imprint","INTERSECT",VERTEX,{"derivedFrom":[subQ18,subQ5,subQ4]}),1.0]])],"derivedFrom":subQ5})])]});var subQ20=sQuery(id+"F3.wireOp",EDGE,"E17");var subQ21=sQuery(id+"F3.wireOp",EDGE,"E32");var subQ22=makeQuery(id+"F13.opExtrude","SWEPT_FACE",FACE,{"disambiguationData":[OSD([subQ5]),TDD([makeQuery(id+"F12.imprint","IMPRINT",EDGE,{"disambiguationData":[TD([[makeQuery(id+"F12.imprint","INTERSECT",VERTEX,{"derivedFrom":[makeQuery(id+"F4.boolean.opBoolean","COPY",EDGE,{"derivedFrom":makeQuery(id+"F4.opExtrude","SWEPT_EDGE",EDGE,{"disambiguationData":[OSD([subQ6,subQ20])]})}),subQ5]}),1.0],[makeQuery(id+"F12.imprint","INTERSECT",VERTEX,{"derivedFrom":[makeQuery(id+"F4.boolean.opBoolean","COPY",EDGE,{"derivedFrom":makeQuery(id+"F4.opExtrude","SWEPT_EDGE",EDGE,{"disambiguationData":[OSD([subQ6,subQ21])]})}),subQ5]}),-1.0]])],"derivedFrom":subQ5})])]});var subQ23=sQuery(id+"F3.wireOp",EDGE,"E8");var subQ24=makeQuery(id+"F13.opExtrude","SWEPT_FACE",FACE,{"disambiguationData":[OSD([subQ5]),TDD([makeQuery(id+"F12.imprint","IMPRINT",EDGE,{"disambiguationData":[TD([[makeQuery(id+"F12.imprint","INTERSECT",VERTEX,{"derivedFrom":[makeQuery(id+"F4.boolean.opBoolean","COPY",EDGE,{"derivedFrom":makeQuery(id+"F4.opExtrude","SWEPT_EDGE",EDGE,{"disambiguationData":[OSD([subQ6,subQ1])]})}),subQ5]}),1.0],[makeQuery(id+"F12.imprint","INTERSECT",VERTEX,{"derivedFrom":[makeQuery(id+"F4.boolean.opBoolean","COPY",EDGE,{"derivedFrom":makeQuery(id+"F4.opExtrude","SWEPT_EDGE",EDGE,{"disambiguationData":[OSD([subQ15,subQ23,subQ6])]})}),subQ5,sQuery(id+"F12.wireOp",EDGE,"E44")]}),-1.0]])],"derivedFrom":subQ5})])]});var subQ25=makeQuery(id+"F11.boolean.opBoolean","COPY",FACE,{"derivedFrom":makeQuery(id+"F11.opExtrude","CAP_FACE",FACE,{"disambiguationData":[OSD([subQ20,subQ3,subQ1,subQ9,subQ21,subQ10,subQ8,subQ7,sQuery(id+"F9.wireOp",EDGE,"E41"),sQuery(id+"F9.wireOp",EDGE,"E42")])],"isStart":false})});Q4=makeQuery(id+"F17.opFillet","BLEND_EDGE",EDGE,{"blendedFrom":[makeQuery(id+"F13.boolean.opBoolean","SPLIT",EDGE,{"disambiguationData":[TD([makeQuery(id+"F1.opExtrude","SWEPT_FACE",FACE,{"disambiguationData":[OSD([sQuery(id+"F0.wireOp",EDGE,"E2")])]})])],"derivedFrom":subQ18}),makeQuery(id+"F16.boolean.opBoolean","MERGE",FACE,{"derivedFrom":[makeQuery(id+"F15.opExtrude","SWEPT_FACE",FACE,{"disambiguationData":[OSD([subQ0]),TDD([makeQuery(id+"F14.imprint","IMPRINT",EDGE,{"disambiguationData":[TD([[makeQuery(id+"F14.imprint","INTERSECT",VERTEX,{"derivedFrom":[makeQuery(id+"F4.boolean.opBoolean","COPY",EDGE,{"derivedFrom":makeQuery(id+"F4.opExtrude","SWEPT_EDGE",EDGE,{"disambiguationData":[OSD([subQ2,subQ1])]})}),subQ0]}),1.0],[makeQuery(id+"F14.imprint","INTERSECT",VERTEX,{"derivedFrom":[makeQuery(id+"F4.boolean.opBoolean","COPY",EDGE,{"derivedFrom":makeQuery(id+"F4.opExtrude","SWEPT_EDGE",EDGE,{"disambiguationData":[OSD([subQ15,subQ14,subQ2])]})}),subQ0,sQuery(id+"F14.wireOp",EDGE,"E50")]}),-1.0]])],"derivedFrom":subQ0})])]}),makeQuery(id+"F15.boolean.opBoolean","MERGE",FACE,{"derivedFrom":[makeQuery(id+"F13.boolean.opBoolean","MERGE",FACE,{"derivedFrom":[subQ25,subQ24,subQ22,subQ19]}),makeQuery(id+"F15.opExtrude","SWEPT_FACE",FACE,{"disambiguationData":[OSD([subQ0]),TDD([makeQuery(id+"F14.imprint","IMPRINT",EDGE,{"disambiguationData":[TD([[makeQuery(id+"F14.imprint","INTERSECT",VERTEX,{"derivedFrom":[makeQuery(id+"F4.boolean.opBoolean","COPY",EDGE,{"derivedFrom":makeQuery(id+"F4.opExtrude","SWEPT_EDGE",EDGE,{"disambiguationData":[OSD([subQ2,subQ9])]})}),subQ0]}),-1.0],[makeQuery(id+"F14.imprint","INTERSECT",VERTEX,{"derivedFrom":[makeQuery(id+"F4.boolean.opBoolean","COPY",EDGE,{"derivedFrom":makeQuery(id+"F4.opExtrude","SWEPT_EDGE",EDGE,{"disambiguationData":[OSD([subQ2,subQ10])]})}),subQ0]}),1.0]])],"derivedFrom":subQ0})])]}),makeQuery(id+"F15.opExtrude","SWEPT_FACE",FACE,{"disambiguationData":[OSD([subQ0]),TDD([makeQuery(id+"F14.imprint","IMPRINT",EDGE,{"disambiguationData":[TD([[makeQuery(id+"F14.imprint","INTERSECT",VERTEX,{"derivedFrom":[makeQuery(id+"F4.boolean.opBoolean","COPY",EDGE,{"derivedFrom":makeQuery(id+"F4.opExtrude","SWEPT_EDGE",EDGE,{"disambiguationData":[OSD([subQ2,subQ3])]})}),subQ0]}),-1.0],[makeQuery(id+"F14.imprint","INTERSECT",VERTEX,{"derivedFrom":[makeQuery(id+"F13.boolean.opBoolean","INTERSECT",EDGE,{"derivedFrom":[makeQuery(id+"F11.boolean.opBoolean","MERGE",FACE,{"derivedFrom":[makeQuery(id+"F7.boolean.opBoolean","MERGE",FACE,{"derivedFrom":[subQ17,subQ13,subQ11],"fromTools":[makeQuery(id+"F7.opExtrude","SWEPT_FACE",FACE,{"disambiguationData":[OSD([sQuery(id+"F6.wireOp",EDGE,"E36")])]}),makeQuery(id+"F7.opExtrude","SWEPT_FACE",FACE,{"disambiguationData":[OSD([sQuery(id+"F6.wireOp",EDGE,"E37")])]})]})],"fromTools":[makeQuery(id+"F11.opExtrude","SWEPT_FACE",FACE,{"disambiguationData":[OSD([subQ8])]}),makeQuery(id+"F11.opExtrude","SWEPT_FACE",FACE,{"disambiguationData":[OSD([subQ7])]})]}),makeQuery(id+"F13.opExtrude","CAP_FACE",FACE,{"disambiguationData":[OSD([subQ6,subQ3,subQ5,sQuery(id+"F12.wireOp",EDGE,"E45"),subQ4])],"isStart":false})]}),subQ0]}),1.0]])],"derivedFrom":subQ0})])]})]}),makeQuery(id+"F16.opExtrude","SWEPT_FACE",FACE,{"disambiguationData":[OSD([subQ2,subQ1,subQ0])]})]})],"blendedInto":[makeQuery(id+"F16.boolean.opBoolean","MERGE",FACE,{"derivedFrom":[makeQuery(id+"F15.opExtrude","SWEPT_FACE",FACE,{"disambiguationData":[OSD([subQ0]),TDD([makeQuery(id+"F14.imprint","IMPRINT",EDGE,{"disambiguationData":[TD([[makeQuery(id+"F14.imprint","INTERSECT",VERTEX,{"derivedFrom":[makeQuery(id+"F4.boolean.opBoolean","COPY",EDGE,{"derivedFrom":makeQuery(id+"F4.opExtrude","SWEPT_EDGE",EDGE,{"disambiguationData":[OSD([subQ2,subQ1])]})}),subQ0]}),1.0],[makeQuery(id+"F14.imprint","INTERSECT",VERTEX,{"derivedFrom":[makeQuery(id+"F4.boolean.opBoolean","COPY",EDGE,{"derivedFrom":makeQuery(id+"F4.opExtrude","SWEPT_EDGE",EDGE,{"disambiguationData":[OSD([subQ15,subQ14,subQ2])]})}),subQ0,sQuery(id+"F14.wireOp",EDGE,"E50")]}),-1.0]])],"derivedFrom":subQ0})])]}),makeQuery(id+"F15.boolean.opBoolean","MERGE",FACE,{"derivedFrom":[makeQuery(id+"F13.boolean.opBoolean","MERGE",FACE,{"derivedFrom":[subQ25,subQ24,subQ22,subQ19]}),makeQuery(id+"F15.opExtrude","SWEPT_FACE",FACE,{"disambiguationData":[OSD([subQ0]),TDD([makeQuery(id+"F14.imprint","IMPRINT",EDGE,{"disambiguationData":[TD([[makeQuery(id+"F14.imprint","INTERSECT",VERTEX,{"derivedFrom":[makeQuery(id+"F4.boolean.opBoolean","COPY",EDGE,{"derivedFrom":makeQuery(id+"F4.opExtrude","SWEPT_EDGE",EDGE,{"disambiguationData":[OSD([subQ2,subQ9])]})}),subQ0]}),-1.0],[makeQuery(id+"F14.imprint","INTERSECT",VERTEX,{"derivedFrom":[makeQuery(id+"F4.boolean.opBoolean","COPY",EDGE,{"derivedFrom":makeQuery(id+"F4.opExtrude","SWEPT_EDGE",EDGE,{"disambiguationData":[OSD([subQ2,subQ10])]})}),subQ0]}),1.0]])],"derivedFrom":subQ0})])]}),makeQuery(id+"F15.opExtrude","SWEPT_FACE",FACE,{"disambiguationData":[OSD([subQ0]),TDD([makeQuery(id+"F14.imprint","IMPRINT",EDGE,{"disambiguationData":[TD([[makeQuery(id+"F14.imprint","INTERSECT",VERTEX,{"derivedFrom":[makeQuery(id+"F4.boolean.opBoolean","COPY",EDGE,{"derivedFrom":makeQuery(id+"F4.opExtrude","SWEPT_EDGE",EDGE,{"disambiguationData":[OSD([subQ2,subQ3])]})}),subQ0]}),-1.0],[makeQuery(id+"F14.imprint","INTERSECT",VERTEX,{"derivedFrom":[makeQuery(id+"F13.boolean.opBoolean","INTERSECT",EDGE,{"derivedFrom":[makeQuery(id+"F11.boolean.opBoolean","MERGE",FACE,{"derivedFrom":[makeQuery(id+"F7.boolean.opBoolean","MERGE",FACE,{"derivedFrom":[subQ17,subQ13,subQ11],"fromTools":[makeQuery(id+"F7.opExtrude","SWEPT_FACE",FACE,{"disambiguationData":[OSD([sQuery(id+"F6.wireOp",EDGE,"E36")])]}),makeQuery(id+"F7.opExtrude","SWEPT_FACE",FACE,{"disambiguationData":[OSD([sQuery(id+"F6.wireOp",EDGE,"E37")])]})]})],"fromTools":[makeQuery(id+"F11.opExtrude","SWEPT_FACE",FACE,{"disambiguationData":[OSD([subQ8])]}),makeQuery(id+"F11.opExtrude","SWEPT_FACE",FACE,{"disambiguationData":[OSD([subQ7])]})]}),makeQuery(id+"F13.opExtrude","CAP_FACE",FACE,{"disambiguationData":[OSD([subQ6,subQ3,subQ5,sQuery(id+"F12.wireOp",EDGE,"E45"),subQ4])],"isStart":false})]}),subQ0]}),1.0]])],"derivedFrom":subQ0})])]})]}),makeQuery(id+"F16.opExtrude","SWEPT_FACE",FACE,{"disambiguationData":[OSD([subQ2,subQ1,subQ0])]})]})]});}
            var Q5;
            {var subQ0=sQuery(id+"F14.wireOp",EDGE,"E47");var subQ1=sQuery(id+"F3.wireOp",EDGE,"E22");var subQ2=sQuery(id+"F3.wireOp",EDGE,"E11");var subQ3=sQuery(id+"F3.wireOp",EDGE,"E18");var subQ5=sQuery(id+"F12.wireOp",EDGE,"E45");var subQ6=sQuery(id+"F3.wireOp",EDGE,"E9");var subQ7=sQuery(id+"F6.wireOp",EDGE,"E37");var subQ8=sQuery(id+"F6.wireOp",EDGE,"E36");var subQ9=sQuery(id+"F3.wireOp",EDGE,"E23");var subQ10=sQuery(id+"F3.wireOp",EDGE,"E33");var subQ15=sQuery(id+"F0.wireOp",EDGE,"E3.MirrorCS");var subQ18=makeQuery(id+"F4.boolean.opBoolean","COPY",EDGE,{"derivedFrom":makeQuery(id+"F4.opExtrude","SWEPT_EDGE",EDGE,{"disambiguationData":[OSD([subQ6,subQ2])]})});var subQ19=makeQuery(id+"F13.opExtrude","SWEPT_FACE",FACE,{"disambiguationData":[OSD([subQ5]),TDD([makeQuery(id+"F12.imprint","IMPRINT",EDGE,{"disambiguationData":[TD([[makeQuery(id+"F12.imprint","INTERSECT",VERTEX,{"derivedFrom":[makeQuery(id+"F4.boolean.opBoolean","COPY",EDGE,{"derivedFrom":makeQuery(id+"F4.opExtrude","SWEPT_EDGE",EDGE,{"disambiguationData":[OSD([subQ6,subQ3])]})}),subQ5]}),-1.0]])],"derivedFrom":subQ5})])]});var subQ20=sQuery(id+"F3.wireOp",EDGE,"E17");var subQ21=sQuery(id+"F3.wireOp",EDGE,"E32");var subQ22=makeQuery(id+"F13.opExtrude","SWEPT_FACE",FACE,{"disambiguationData":[OSD([subQ5]),TDD([makeQuery(id+"F12.imprint","IMPRINT",EDGE,{"disambiguationData":[TD([[makeQuery(id+"F12.imprint","INTERSECT",VERTEX,{"derivedFrom":[makeQuery(id+"F4.boolean.opBoolean","COPY",EDGE,{"derivedFrom":makeQuery(id+"F4.opExtrude","SWEPT_EDGE",EDGE,{"disambiguationData":[OSD([subQ6,subQ20])]})}),subQ5]}),1.0]])],"derivedFrom":subQ5})])]});var subQ24=makeQuery(id+"F13.opExtrude","SWEPT_FACE",FACE,{"disambiguationData":[OSD([subQ5]),TDD([makeQuery(id+"F12.imprint","IMPRINT",EDGE,{"disambiguationData":[TD([[makeQuery(id+"F12.imprint","INTERSECT",VERTEX,{"derivedFrom":[makeQuery(id+"F4.boolean.opBoolean","COPY",EDGE,{"derivedFrom":makeQuery(id+"F4.opExtrude","SWEPT_EDGE",EDGE,{"disambiguationData":[OSD([subQ6,subQ1])]})}),subQ5]}),1.0]])],"derivedFrom":subQ5})])]});var subQ25=makeQuery(id+"F7.boolean.opBoolean","COPY",FACE,{"derivedFrom":makeQuery(id+"F7.opExtrude","CAP_FACE",FACE,{"disambiguationData":[OSD([subQ20,subQ3,subQ1,subQ9,subQ21,subQ10,sQuery(id+"F6.wireOp",EDGE,"E34"),sQuery(id+"F6.wireOp",EDGE,"E35"),subQ8,subQ7])],"isStart":false})});Q5=makeQuery(id+"F17.opFillet","BLEND_EDGE",EDGE,{"blendedFrom":[makeQuery(id+"F13.boolean.opBoolean","SPLIT",EDGE,{"disambiguationData":[TD([makeQuery(id+"F1.opExtrude","SWEPT_FACE",FACE,{"disambiguationData":[OSD([subQ15])]})])],"derivedFrom":subQ18}),makeQuery(id+"F16.boolean.opBoolean","MERGE",FACE,{"derivedFrom":[makeQuery(id+"F15.opExtrude","SWEPT_FACE",FACE,{"disambiguationData":[OSD([subQ0]),TDD([makeQuery(id+"F14.imprint","IMPRINT",EDGE,{"disambiguationData":[TD([[makeQuery(id+"F14.imprint","INTERSECT",VERTEX,{"derivedFrom":[makeQuery(id+"F4.boolean.opBoolean","COPY",EDGE,{"derivedFrom":makeQuery(id+"F4.opExtrude","SWEPT_EDGE",EDGE,{"disambiguationData":[OSD([subQ2,subQ1])]})}),subQ0]}),1.0]])],"derivedFrom":subQ0})])]}),makeQuery(id+"F15.boolean.opBoolean","MERGE",FACE,{"derivedFrom":[makeQuery(id+"F13.boolean.opBoolean","MERGE",FACE,{"derivedFrom":[subQ25,subQ24,subQ22,subQ19]}),makeQuery(id+"F15.opExtrude","SWEPT_FACE",FACE,{"disambiguationData":[OSD([subQ0]),TDD([makeQuery(id+"F14.imprint","IMPRINT",EDGE,{"disambiguationData":[TD([[makeQuery(id+"F14.imprint","INTERSECT",VERTEX,{"derivedFrom":[makeQuery(id+"F4.boolean.opBoolean","COPY",EDGE,{"derivedFrom":makeQuery(id+"F4.opExtrude","SWEPT_EDGE",EDGE,{"disambiguationData":[OSD([subQ2,subQ9])]})}),subQ0]}),-1.0]])],"derivedFrom":subQ0})])]}),makeQuery(id+"F15.opExtrude","SWEPT_FACE",FACE,{"disambiguationData":[OSD([subQ0]),TDD([makeQuery(id+"F14.imprint","IMPRINT",EDGE,{"disambiguationData":[TD([[makeQuery(id+"F14.imprint","INTERSECT",VERTEX,{"derivedFrom":[makeQuery(id+"F4.boolean.opBoolean","COPY",EDGE,{"derivedFrom":makeQuery(id+"F4.opExtrude","SWEPT_EDGE",EDGE,{"disambiguationData":[OSD([subQ2,subQ3])]})}),subQ0]}),-1.0]])],"derivedFrom":subQ0})])]})]}),makeQuery(id+"F16.opExtrude","SWEPT_FACE",FACE,{"disambiguationData":[OSD([subQ2,subQ1,subQ0])]})]})],"blendedInto":[makeQuery(id+"F16.boolean.opBoolean","MERGE",FACE,{"derivedFrom":[makeQuery(id+"F15.opExtrude","SWEPT_FACE",FACE,{"disambiguationData":[OSD([subQ0]),TDD([makeQuery(id+"F14.imprint","IMPRINT",EDGE,{"disambiguationData":[TD([[makeQuery(id+"F14.imprint","INTERSECT",VERTEX,{"derivedFrom":[makeQuery(id+"F4.boolean.opBoolean","COPY",EDGE,{"derivedFrom":makeQuery(id+"F4.opExtrude","SWEPT_EDGE",EDGE,{"disambiguationData":[OSD([subQ2,subQ1])]})}),subQ0]}),1.0]])],"derivedFrom":subQ0})])]}),makeQuery(id+"F15.boolean.opBoolean","MERGE",FACE,{"derivedFrom":[makeQuery(id+"F13.boolean.opBoolean","MERGE",FACE,{"derivedFrom":[subQ25,subQ24,subQ22,subQ19]}),makeQuery(id+"F15.opExtrude","SWEPT_FACE",FACE,{"disambiguationData":[OSD([subQ0]),TDD([makeQuery(id+"F14.imprint","IMPRINT",EDGE,{"disambiguationData":[TD([[makeQuery(id+"F14.imprint","INTERSECT",VERTEX,{"derivedFrom":[makeQuery(id+"F4.boolean.opBoolean","COPY",EDGE,{"derivedFrom":makeQuery(id+"F4.opExtrude","SWEPT_EDGE",EDGE,{"disambiguationData":[OSD([subQ2,subQ9])]})}),subQ0]}),-1.0]])],"derivedFrom":subQ0})])]}),makeQuery(id+"F15.opExtrude","SWEPT_FACE",FACE,{"disambiguationData":[OSD([subQ0]),TDD([makeQuery(id+"F14.imprint","IMPRINT",EDGE,{"disambiguationData":[TD([[makeQuery(id+"F14.imprint","INTERSECT",VERTEX,{"derivedFrom":[makeQuery(id+"F4.boolean.opBoolean","COPY",EDGE,{"derivedFrom":makeQuery(id+"F4.opExtrude","SWEPT_EDGE",EDGE,{"disambiguationData":[OSD([subQ2,subQ3])]})}),subQ0]}),-1.0]])],"derivedFrom":subQ0})])]})]}),makeQuery(id+"F16.opExtrude","SWEPT_FACE",FACE,{"disambiguationData":[OSD([subQ2,subQ1,subQ0])]})]})]});}
            fillet(context, id + "F19", {"entities" : qUnion([Q0, Q1, Q2, Q3, Q4, Q5]), "radius" : 1 * mm, "tangentPropagation" : true, "allowEdgeOverflow" : false});
        }
        {
            var Q0;
            {var subQ0=sQuery(id+"F3.wireOp",EDGE,"E9");Q0=makeQuery(id+"F7.boolean.opBoolean","MERGE",EDGE,{"derivedFrom":[makeQuery(id+"F4.boolean.opBoolean","COPY",EDGE,{"derivedFrom":makeQuery(id+"F4.opExtrude","CAP_EDGE",EDGE,{"disambiguationData":[OSD([subQ0]),TDD([makeQuery(id+"F3.imprint","IMPRINT",EDGE,{"disambiguationData":[TD([[makeQuery(id+"F3.imprint","INTERSECT",VERTEX,{"derivedFrom":[subQ0,sQuery(id+"F3.wireOp",EDGE,"E22")]}),1.0]])],"derivedFrom":subQ0})])],"isStart":true})}),makeQuery(id+"F4.boolean.opBoolean","COPY",EDGE,{"derivedFrom":makeQuery(id+"F4.opExtrude","CAP_EDGE",EDGE,{"disambiguationData":[OSD([subQ0]),TDD([makeQuery(id+"F3.imprint","IMPRINT",EDGE,{"disambiguationData":[TD([[makeQuery(id+"F3.imprint","INTERSECT",VERTEX,{"derivedFrom":[subQ0,sQuery(id+"F3.wireOp",EDGE,"E18")]}),-1.0]])],"derivedFrom":subQ0})])],"isStart":true})}),makeQuery(id+"F4.boolean.opBoolean","COPY",EDGE,{"derivedFrom":makeQuery(id+"F4.opExtrude","CAP_EDGE",EDGE,{"disambiguationData":[OSD([subQ0]),TDD([makeQuery(id+"F3.imprint","IMPRINT",EDGE,{"disambiguationData":[TD([[makeQuery(id+"F3.imprint","INTERSECT",VERTEX,{"derivedFrom":[subQ0,sQuery(id+"F3.wireOp",EDGE,"E17")]}),1.0]])],"derivedFrom":subQ0})])],"isStart":true})})],"fromTools":[makeQuery(id+"F7.opExtrude","CAP_EDGE",EDGE,{"disambiguationData":[OSD([sQuery(id+"F6.wireOp",EDGE,"E34")])],"isStart":true}),makeQuery(id+"F7.opExtrude","CAP_EDGE",EDGE,{"disambiguationData":[OSD([sQuery(id+"F6.wireOp",EDGE,"E35")])],"isStart":true})]});}
            var Q1;
            Q1=makeQuery(id+"F1.opExtrude","SWEPT_EDGE",EDGE,{"disambiguationData":[OSD([sQuery(id+"F0.wireOp",EDGE,"E0"),sQuery(id+"F0.wireOp",EDGE,"E3.MirrorCS")])]});
            var Q2;
            Q2=makeQuery(id+"F1.opExtrude","SWEPT_EDGE",EDGE,{"disambiguationData":[OSD([sQuery(id+"F0.wireOp",EDGE,"E1.MirrorCS"),sQuery(id+"F0.wireOp",EDGE,"E2")])]});
            var Q3;
            {var subQ0=sQuery(id+"F3.wireOp",EDGE,"E9");Q3=makeQuery(id+"F11.boolean.opBoolean","MERGE",EDGE,{"derivedFrom":[makeQuery(id+"F4.boolean.opBoolean","COPY",EDGE,{"derivedFrom":makeQuery(id+"F4.opExtrude","CAP_EDGE",EDGE,{"disambiguationData":[OSD([subQ0]),TDD([makeQuery(id+"F3.imprint","IMPRINT",EDGE,{"disambiguationData":[TD([[makeQuery(id+"F3.imprint","INTERSECT",VERTEX,{"derivedFrom":[subQ0,sQuery(id+"F3.wireOp",EDGE,"E22")]}),1.0]])],"derivedFrom":subQ0})])],"isStart":false})}),makeQuery(id+"F4.boolean.opBoolean","COPY",EDGE,{"derivedFrom":makeQuery(id+"F4.opExtrude","CAP_EDGE",EDGE,{"disambiguationData":[OSD([subQ0]),TDD([makeQuery(id+"F3.imprint","IMPRINT",EDGE,{"disambiguationData":[TD([[makeQuery(id+"F3.imprint","INTERSECT",VERTEX,{"derivedFrom":[subQ0,sQuery(id+"F3.wireOp",EDGE,"E18")]}),-1.0]])],"derivedFrom":subQ0})])],"isStart":false})}),makeQuery(id+"F4.boolean.opBoolean","COPY",EDGE,{"derivedFrom":makeQuery(id+"F4.opExtrude","CAP_EDGE",EDGE,{"disambiguationData":[OSD([subQ0]),TDD([makeQuery(id+"F3.imprint","IMPRINT",EDGE,{"disambiguationData":[TD([[makeQuery(id+"F3.imprint","INTERSECT",VERTEX,{"derivedFrom":[subQ0,sQuery(id+"F3.wireOp",EDGE,"E17")]}),1.0]])],"derivedFrom":subQ0})])],"isStart":false})})],"fromTools":[makeQuery(id+"F11.opExtrude","CAP_EDGE",EDGE,{"disambiguationData":[OSD([sQuery(id+"F9.wireOp",EDGE,"E41")])],"isStart":true}),makeQuery(id+"F11.opExtrude","CAP_EDGE",EDGE,{"disambiguationData":[OSD([sQuery(id+"F9.wireOp",EDGE,"E42")])],"isStart":true})]});}
            var Q4;
            {var subQ0=sQuery(id+"F3.wireOp",EDGE,"E12");var subQ2=makeQuery(id+"F3.imprint","INTERSECT",VERTEX,{"derivedFrom":[subQ0,sQuery(id+"F3.wireOp",EDGE,"E24")]});Q4=makeQuery(id+"F5.boolean.opBoolean","COPY",EDGE,{"derivedFrom":makeQuery(id+"F5.opExtrude","TWEAK_EDGE",EDGE,{"derivedFrom":[makeQuery(id+"F3.imprint","IMPRINT",EDGE,{"disambiguationData":[TD([[subQ2,1.0]])],"derivedFrom":subQ0}),makeQuery(id+"F3.imprint","IMPRINT",EDGE,{"disambiguationData":[TD([[subQ2,-1.0]])],"derivedFrom":subQ0}),makeQuery(id+"F1.opExtrude","SWEPT_FACE",FACE,{"disambiguationData":[OSD([sQuery(id+"F0.wireOp",EDGE,"E2")])]})]})});}
            var Q5;
            Q5=makeQuery(id+"F5.boolean.opBoolean","COPY",EDGE,{"derivedFrom":makeQuery(id+"F5.opExtrude","CAP_EDGE",EDGE,{"disambiguationData":[OSD([sQuery(id+"F3.wireOp",EDGE,"E12")])],"isStart":true})});
            fillet(context, id + "F20", {"entities" : qUnion([Q0, Q1, Q2, Q3, Q4, Q5]), "radius" : 2 * mm, "tangentPropagation" : true, "allowEdgeOverflow" : false});
        }
        {
            var Q0;
            {var subQ0=sQuery(id+"F14.wireOp",EDGE,"E48");var subQ1=sQuery(id+"F3.wireOp",EDGE,"E22");var subQ2=sQuery(id+"F3.wireOp",EDGE,"E11");Q0=makeQuery(id+"F16.boolean.opBoolean","MERGE",EDGE,{"derivedFrom":[makeQuery(id+"F15.opExtrude","CAP_EDGE",EDGE,{"disambiguationData":[OSD([subQ0]),TDD([makeQuery(id+"F14.imprint","IMPRINT",EDGE,{"disambiguationData":[TD([[makeQuery(id+"F14.imprint","INTERSECT",VERTEX,{"derivedFrom":[makeQuery(id+"F4.boolean.opBoolean","COPY",EDGE,{"derivedFrom":makeQuery(id+"F4.opExtrude","SWEPT_EDGE",EDGE,{"disambiguationData":[OSD([subQ2,subQ1])]})}),subQ0]}),1.0],[makeQuery(id+"F14.imprint","INTERSECT",VERTEX,{"derivedFrom":[makeQuery(id+"F4.boolean.opBoolean","COPY",EDGE,{"derivedFrom":makeQuery(id+"F4.opExtrude","SWEPT_EDGE",EDGE,{"disambiguationData":[OSD([sQuery(id+"F0.wireOp",EDGE,"E3.MirrorCS"),sQuery(id+"F3.wireOp",EDGE,"E10"),subQ2])]})}),subQ0,sQuery(id+"F14.wireOp",EDGE,"E50")]}),-1.0]])],"derivedFrom":subQ0})])],"isStart":false}),makeQuery(id+"F16.opExtrude","SWEPT_EDGE",EDGE,{"disambiguationData":[OSD([subQ2,subQ1,subQ0])]})]});}
            var Q1;
            {var subQ0=sQuery(id+"F14.wireOp",EDGE,"E47");var subQ1=sQuery(id+"F3.wireOp",EDGE,"E22");var subQ2=sQuery(id+"F3.wireOp",EDGE,"E11");Q1=makeQuery(id+"F16.boolean.opBoolean","MERGE",EDGE,{"derivedFrom":[makeQuery(id+"F15.opExtrude","CAP_EDGE",EDGE,{"disambiguationData":[OSD([subQ0]),TDD([makeQuery(id+"F14.imprint","IMPRINT",EDGE,{"disambiguationData":[TD([[makeQuery(id+"F14.imprint","INTERSECT",VERTEX,{"derivedFrom":[makeQuery(id+"F4.boolean.opBoolean","COPY",EDGE,{"derivedFrom":makeQuery(id+"F4.opExtrude","SWEPT_EDGE",EDGE,{"disambiguationData":[OSD([subQ2,subQ1])]})}),subQ0]}),1.0]])],"derivedFrom":subQ0})])],"isStart":false}),makeQuery(id+"F16.opExtrude","SWEPT_EDGE",EDGE,{"disambiguationData":[OSD([subQ2,subQ1,subQ0])]})]});}
            var Q2;
            {var subQ0=sQuery(id+"F14.wireOp",EDGE,"E48");var subQ1=sQuery(id+"F3.wireOp",EDGE,"E11");Q2=makeQuery(id+"F15.opExtrude","CAP_EDGE",EDGE,{"disambiguationData":[OSD([subQ0]),TDD([makeQuery(id+"F14.imprint","IMPRINT",EDGE,{"disambiguationData":[TD([[makeQuery(id+"F14.imprint","INTERSECT",VERTEX,{"derivedFrom":[makeQuery(id+"F4.boolean.opBoolean","COPY",EDGE,{"derivedFrom":makeQuery(id+"F4.opExtrude","SWEPT_EDGE",EDGE,{"disambiguationData":[OSD([subQ1,sQuery(id+"F3.wireOp",EDGE,"E23")])]})}),subQ0]}),-1.0],[makeQuery(id+"F14.imprint","INTERSECT",VERTEX,{"derivedFrom":[makeQuery(id+"F4.boolean.opBoolean","COPY",EDGE,{"derivedFrom":makeQuery(id+"F4.opExtrude","SWEPT_EDGE",EDGE,{"disambiguationData":[OSD([subQ1,sQuery(id+"F3.wireOp",EDGE,"E33")])]})}),subQ0]}),1.0]])],"derivedFrom":subQ0})])],"isStart":false});}
            var Q3;
            {var subQ0=sQuery(id+"F14.wireOp",EDGE,"E47");var subQ1=sQuery(id+"F3.wireOp",EDGE,"E11");Q3=makeQuery(id+"F15.opExtrude","CAP_EDGE",EDGE,{"disambiguationData":[OSD([subQ0]),TDD([makeQuery(id+"F14.imprint","IMPRINT",EDGE,{"disambiguationData":[TD([[makeQuery(id+"F14.imprint","INTERSECT",VERTEX,{"derivedFrom":[makeQuery(id+"F4.boolean.opBoolean","COPY",EDGE,{"derivedFrom":makeQuery(id+"F4.opExtrude","SWEPT_EDGE",EDGE,{"disambiguationData":[OSD([subQ1,sQuery(id+"F3.wireOp",EDGE,"E23")])]})}),subQ0]}),-1.0]])],"derivedFrom":subQ0})])],"isStart":false});}
            var Q4;
            {var subQ0=sQuery(id+"F14.wireOp",EDGE,"E48");var subQ1=sQuery(id+"F3.wireOp",EDGE,"E18");var subQ2=sQuery(id+"F3.wireOp",EDGE,"E11");var subQ3=sQuery(id+"F3.wireOp",EDGE,"E9");Q4=makeQuery(id+"F15.opExtrude","CAP_EDGE",EDGE,{"disambiguationData":[OSD([subQ0]),TDD([makeQuery(id+"F14.imprint","IMPRINT",EDGE,{"disambiguationData":[TD([[makeQuery(id+"F14.imprint","INTERSECT",VERTEX,{"derivedFrom":[makeQuery(id+"F4.boolean.opBoolean","COPY",EDGE,{"derivedFrom":makeQuery(id+"F4.opExtrude","SWEPT_EDGE",EDGE,{"disambiguationData":[OSD([subQ2,subQ1])]})}),subQ0]}),-1.0],[makeQuery(id+"F14.imprint","INTERSECT",VERTEX,{"derivedFrom":[makeQuery(id+"F13.boolean.opBoolean","INTERSECT",EDGE,{"derivedFrom":[makeQuery(id+"F11.boolean.opBoolean","MERGE",FACE,{"derivedFrom":[makeQuery(id+"F7.boolean.opBoolean","MERGE",FACE,{"derivedFrom":[makeQuery(id+"F4.boolean.opBoolean","COPY",FACE,{"derivedFrom":makeQuery(id+"F4.opExtrude","SWEPT_FACE",FACE,{"disambiguationData":[OSD([subQ2]),TDD([makeQuery(id+"F3.imprint","IMPRINT",EDGE,{"disambiguationData":[TD([[makeQuery(id+"F3.imprint","INTERSECT",VERTEX,{"derivedFrom":[subQ2,sQuery(id+"F3.wireOp",EDGE,"E22")]}),1.0]])],"derivedFrom":subQ2})])]})}),makeQuery(id+"F4.boolean.opBoolean","COPY",FACE,{"derivedFrom":makeQuery(id+"F4.opExtrude","SWEPT_FACE",FACE,{"disambiguationData":[OSD([subQ2]),TDD([makeQuery(id+"F3.imprint","IMPRINT",EDGE,{"disambiguationData":[TD([[makeQuery(id+"F3.imprint","INTERSECT",VERTEX,{"derivedFrom":[subQ2,subQ1]}),-1.0]])],"derivedFrom":subQ2})])]})}),makeQuery(id+"F4.boolean.opBoolean","COPY",FACE,{"derivedFrom":makeQuery(id+"F4.opExtrude","SWEPT_FACE",FACE,{"disambiguationData":[OSD([subQ2]),TDD([makeQuery(id+"F3.imprint","IMPRINT",EDGE,{"disambiguationData":[TD([[makeQuery(id+"F3.imprint","INTERSECT",VERTEX,{"derivedFrom":[subQ2,sQuery(id+"F3.wireOp",EDGE,"E23")]}),-1.0]])],"derivedFrom":subQ2})])]})})],"fromTools":[makeQuery(id+"F7.opExtrude","SWEPT_FACE",FACE,{"disambiguationData":[OSD([sQuery(id+"F6.wireOp",EDGE,"E36")])]}),makeQuery(id+"F7.opExtrude","SWEPT_FACE",FACE,{"disambiguationData":[OSD([sQuery(id+"F6.wireOp",EDGE,"E37")])]})]})],"fromTools":[makeQuery(id+"F11.opExtrude","SWEPT_FACE",FACE,{"disambiguationData":[OSD([sQuery(id+"F9.wireOp",EDGE,"E39")])]}),makeQuery(id+"F11.opExtrude","SWEPT_FACE",FACE,{"disambiguationData":[OSD([sQuery(id+"F9.wireOp",EDGE,"E40")])]})]}),makeQuery(id+"F13.opExtrude","CAP_FACE",FACE,{"disambiguationData":[OSD([subQ3,subQ1,sQuery(id+"F12.wireOp",EDGE,"E43"),sQuery(id+"F12.wireOp",EDGE,"E45"),sQuery(id+"F12.wireOp",EDGE,"E46")])],"isStart":false})]}),subQ0]}),1.0]])],"derivedFrom":subQ0})])],"isStart":false});}
            var Q5;
            {var subQ0=sQuery(id+"F14.wireOp",EDGE,"E47");var subQ1=sQuery(id+"F3.wireOp",EDGE,"E18");var subQ2=sQuery(id+"F3.wireOp",EDGE,"E11");Q5=makeQuery(id+"F15.opExtrude","CAP_EDGE",EDGE,{"disambiguationData":[OSD([subQ0]),TDD([makeQuery(id+"F14.imprint","IMPRINT",EDGE,{"disambiguationData":[TD([[makeQuery(id+"F14.imprint","INTERSECT",VERTEX,{"derivedFrom":[makeQuery(id+"F4.boolean.opBoolean","COPY",EDGE,{"derivedFrom":makeQuery(id+"F4.opExtrude","SWEPT_EDGE",EDGE,{"disambiguationData":[OSD([subQ2,subQ1])]})}),subQ0]}),-1.0]])],"derivedFrom":subQ0})])],"isStart":false});}
            var Q6;
            {var subQ0=sQuery(id+"F12.wireOp",EDGE,"E45");var subQ1=sQuery(id+"F3.wireOp",EDGE,"E9");Q6=makeQuery(id+"F13.opExtrude","CAP_EDGE",EDGE,{"disambiguationData":[OSD([subQ0]),TDD([makeQuery(id+"F12.imprint","IMPRINT",EDGE,{"disambiguationData":[TD([[makeQuery(id+"F12.imprint","INTERSECT",VERTEX,{"derivedFrom":[makeQuery(id+"F4.boolean.opBoolean","COPY",EDGE,{"derivedFrom":makeQuery(id+"F4.opExtrude","SWEPT_EDGE",EDGE,{"disambiguationData":[OSD([subQ1,sQuery(id+"F3.wireOp",EDGE,"E18")])]})}),subQ0]}),-1.0]])],"derivedFrom":subQ0})])],"isStart":false});}
            var Q7;
            {var subQ0=sQuery(id+"F12.wireOp",EDGE,"E43");var subQ1=sQuery(id+"F3.wireOp",EDGE,"E9");Q7=makeQuery(id+"F13.opExtrude","CAP_EDGE",EDGE,{"disambiguationData":[OSD([subQ0]),TDD([makeQuery(id+"F12.imprint","IMPRINT",EDGE,{"disambiguationData":[TD([[makeQuery(id+"F12.imprint","INTERSECT",VERTEX,{"derivedFrom":[makeQuery(id+"F4.boolean.opBoolean","COPY",EDGE,{"derivedFrom":makeQuery(id+"F4.opExtrude","SWEPT_EDGE",EDGE,{"disambiguationData":[OSD([subQ1,sQuery(id+"F3.wireOp",EDGE,"E18")])]})}),subQ0]}),-1.0],[makeQuery(id+"F12.imprint","INTERSECT",VERTEX,{"derivedFrom":[makeQuery(id+"F4.boolean.opBoolean","COPY",EDGE,{"derivedFrom":makeQuery(id+"F4.opExtrude","SWEPT_EDGE",EDGE,{"disambiguationData":[OSD([subQ1,sQuery(id+"F3.wireOp",EDGE,"E11")])]})}),subQ0,sQuery(id+"F12.wireOp",EDGE,"E46")]}),1.0]])],"derivedFrom":subQ0})])],"isStart":false});}
            var Q8;
            {var subQ0=sQuery(id+"F12.wireOp",EDGE,"E43");var subQ1=sQuery(id+"F3.wireOp",EDGE,"E9");Q8=makeQuery(id+"F13.opExtrude","CAP_EDGE",EDGE,{"disambiguationData":[OSD([subQ0]),TDD([makeQuery(id+"F12.imprint","IMPRINT",EDGE,{"disambiguationData":[TD([[makeQuery(id+"F12.imprint","INTERSECT",VERTEX,{"derivedFrom":[makeQuery(id+"F4.boolean.opBoolean","COPY",EDGE,{"derivedFrom":makeQuery(id+"F4.opExtrude","SWEPT_EDGE",EDGE,{"disambiguationData":[OSD([subQ1,sQuery(id+"F3.wireOp",EDGE,"E22")])]})}),subQ0]}),1.0],[makeQuery(id+"F12.imprint","INTERSECT",VERTEX,{"derivedFrom":[makeQuery(id+"F4.boolean.opBoolean","COPY",EDGE,{"derivedFrom":makeQuery(id+"F4.opExtrude","SWEPT_EDGE",EDGE,{"disambiguationData":[OSD([sQuery(id+"F0.wireOp",EDGE,"E3.MirrorCS"),sQuery(id+"F3.wireOp",EDGE,"E8"),subQ1])]})}),subQ0,sQuery(id+"F12.wireOp",EDGE,"E44")]}),-1.0]])],"derivedFrom":subQ0})])],"isStart":false});}
            var Q9;
            {var subQ0=sQuery(id+"F12.wireOp",EDGE,"E45");var subQ1=sQuery(id+"F3.wireOp",EDGE,"E9");Q9=makeQuery(id+"F13.opExtrude","CAP_EDGE",EDGE,{"disambiguationData":[OSD([subQ0]),TDD([makeQuery(id+"F12.imprint","IMPRINT",EDGE,{"disambiguationData":[TD([[makeQuery(id+"F12.imprint","INTERSECT",VERTEX,{"derivedFrom":[makeQuery(id+"F4.boolean.opBoolean","COPY",EDGE,{"derivedFrom":makeQuery(id+"F4.opExtrude","SWEPT_EDGE",EDGE,{"disambiguationData":[OSD([subQ1,sQuery(id+"F3.wireOp",EDGE,"E22")])]})}),subQ0]}),1.0]])],"derivedFrom":subQ0})])],"isStart":false});}
            var Q10;
            {var subQ0=sQuery(id+"F12.wireOp",EDGE,"E43");var subQ1=sQuery(id+"F3.wireOp",EDGE,"E9");Q10=makeQuery(id+"F13.opExtrude","CAP_EDGE",EDGE,{"disambiguationData":[OSD([subQ0]),TDD([makeQuery(id+"F12.imprint","IMPRINT",EDGE,{"disambiguationData":[TD([[makeQuery(id+"F12.imprint","INTERSECT",VERTEX,{"derivedFrom":[makeQuery(id+"F4.boolean.opBoolean","COPY",EDGE,{"derivedFrom":makeQuery(id+"F4.opExtrude","SWEPT_EDGE",EDGE,{"disambiguationData":[OSD([subQ1,sQuery(id+"F3.wireOp",EDGE,"E17")])]})}),subQ0]}),1.0],[makeQuery(id+"F12.imprint","INTERSECT",VERTEX,{"derivedFrom":[makeQuery(id+"F4.boolean.opBoolean","COPY",EDGE,{"derivedFrom":makeQuery(id+"F4.opExtrude","SWEPT_EDGE",EDGE,{"disambiguationData":[OSD([subQ1,sQuery(id+"F3.wireOp",EDGE,"E32")])]})}),subQ0]}),-1.0]])],"derivedFrom":subQ0})])],"isStart":false});}
            var Q11;
            {var subQ0=sQuery(id+"F12.wireOp",EDGE,"E45");var subQ1=sQuery(id+"F3.wireOp",EDGE,"E9");Q11=makeQuery(id+"F13.opExtrude","CAP_EDGE",EDGE,{"disambiguationData":[OSD([subQ0]),TDD([makeQuery(id+"F12.imprint","IMPRINT",EDGE,{"disambiguationData":[TD([[makeQuery(id+"F12.imprint","INTERSECT",VERTEX,{"derivedFrom":[makeQuery(id+"F4.boolean.opBoolean","COPY",EDGE,{"derivedFrom":makeQuery(id+"F4.opExtrude","SWEPT_EDGE",EDGE,{"disambiguationData":[OSD([subQ1,sQuery(id+"F3.wireOp",EDGE,"E17")])]})}),subQ0]}),1.0]])],"derivedFrom":subQ0})])],"isStart":false});}
            fillet(context, id + "F21", {"entities" : qUnion([Q0, Q1, Q2, Q3, Q4, Q5, Q6, Q7, Q8, Q9, Q10, Q11]), "radius" : 1 * mm, "tangentPropagation" : true, "allowEdgeOverflow" : false});
        }
        {
            var Q0;
            {var subQ0=sQuery(id+"F0.wireOp",EDGE,"E2");var subQ1=sQuery(id+"F0.wireOp",EDGE,"E3.MirrorCS");var subQ2=sQuery(id+"F0.wireOp",EDGE,"E4");Q0=makeQuery(id+"F4.boolean.opBoolean","SPLIT",FACE,{"disambiguationData":[TD([makeQuery(id+"F1.opExtrude","SWEPT_FACE",FACE,{"disambiguationData":[OSD([subQ2])]})])],"derivedFrom":makeQuery(id+"F1.opExtrude","CAP_FACE",FACE,{"disambiguationData":[OSD([sQuery(id+"F0.wireOp",EDGE,"E0"),sQuery(id+"F0.wireOp",EDGE,"E1.MirrorCS"),subQ0,subQ1,subQ2])],"isStart":true})});}
            var sketch = newSketch(context, id + "F22", { "sketchPlane" : qUnion([Q0])});
            skLineSegment(sketch, "E51.bottom", {"start": v(2.5, -195) * mm, "end": v(-3.07, -195) * mm});
            skLineSegment(sketch, "E51.top", {"start": v(2.5, -191.31) * mm, "end": v(-3.07, -191.31) * mm});
            skLineSegment(sketch, "E51.left", {"start": v(2.5, -195) * mm, "end": v(2.5, -191.31) * mm});
            skLineSegment(sketch, "E51.right", {"start": v(-3.07, -195) * mm, "end": v(-3.07, -191.31) * mm});
            skSolve(sketch);
        }
        {
            var Q0;
            Q0=qSketchRegion(id+"F22",true);
            extrude(context, id + "F23", {"entities" : qUnion([Q0]), "operationType" : NewBodyOperationType.REMOVE, "depth" : 25 * mm, "offsetDistance" : 25 * mm});
        }
    });
